# Revit family: 879-103X99-001-DN50-250
name_source: partatom
category: Pipe Accessories
units: mm (PartAtom-declared; Revit-internal decimal feet)

## family parameters
Always vertical = Yes
Cut with Voids When Loaded = No
Part Type = Valve - Breaks Into
Round Connector Dimension = Use Diameter
Shared = No
Work Plane-Based = No

## types (45) — shared parameters
879-0050-10-14400309999 = DN50_PN10/16
879-0050-10-14400319999 = DN50_PN10/16
879-0050-10-144003199A0 = DN50_PN10/16
879-0050-10-14400329999 = DN50_PN10/16
879-0050-10-14400339999 = DN50_PN10/16
879-0065-10-14400309999 = DN65_PN10/16
879-0065-10-14400319999 = DN65_PN10/16
879-0065-10-144003199A0 = DN65_PN10/16
879-0065-10-14400329999 = DN65_PN10/16
879-0065-10-14400339999 = DN65_PN10/16
879-0080-10-14400309999 = DN80_PN10/16
879-0080-10-14400319999 = DN80_PN10/16
879-0080-10-144003199A0 = DN80_PN10/16
879-0080-10-14400329999 = DN80_PN10/16
879-0080-10-14400339999 = DN80_PN10/16
879-0100-10-14400309999 = DN100_PN10/16
879-0100-10-14400319999 = DN100_PN10/16
879-0100-10-144003199A0 = DN100_PN10/16
879-0100-10-14400329999 = DN100_PN10/16
879-0100-10-14400339999 = DN100_PN10/16
879-0150-10-14400309999 = DN150_PN10/16
879-0150-10-14400319999 = DN150_PN10/16
879-0150-10-144003199A0 = DN150_PN10/16
879-0150-10-14400329999 = DN150_PN10/16
879-0150-10-14400339999 = DN150_PN10/16
879-0200-10-04400309999 = DN200_PN10
879-0200-10-04400319999 = DN200_PN10
879-0200-10-044003199A0 = DN200_PN10
879-0200-10-04400329999 = DN200_PN10
879-0200-10-04400339999 = DN200_PN10
879-0200-10-14400309999 = DN200_PN16
879-0200-10-14400319999 = DN200_PN16
879-0200-10-144003199A0 = DN200_PN16
879-0200-10-14400329999 = DN200_PN16
879-0200-10-14400339999 = DN200_PN16
879-0250-10-04400309999 = DN250_PN10
879-0250-10-04400319999 = DN250_PN10
879-0250-10-044003199A0 = DN250_PN10
879-0250-10-04400329999 = DN250_PN10
879-0250-10-04400339999 = DN250_PN10
879-0250-10-14400309999 = DN250_PN16
879-0250-10-14400319999 = DN250_PN16
879-0250-10-144003199A0 = DN250_PN16
879-0250-10-14400329999 = DN250_PN16
879-0250-10-14400339999 = DN250_PN16
Body_wall_thickness = 10 mm  [stored 0.0328084 ft]
Description_ = AVK ONE WAY ALTITUDE LEVEL CONTROL VALVE
Search_Table = 879-103X99-001-DN50-250
URL product pages = https://www.avkvalves.com

## per-type parameters (varying)
- 879-0050-10-14400309999_DN50_PN10/16: Body_Collar_Dia=21 mm  [stored 0.0688976 ft]; Body_Collar_Dia_2=14 mm  [stored 0.0459318 ft]; Body_Flange_Dia=66 mm; Body_Flange_Dia_2=72 mm; Body_Height_1=58 mm; Body_Height_2=29 mm; Body_Height_3=45 mm  [stored 0.147638 ft]; Body_Height_4=44 mm  [stored 0.144357 ft]; Body_Top_Dia=9 mm  [stored 0.0295276 ft]; Body_Top_Dia_2=7 mm  [stored 0.0229659 ft]; Body_With_Dia=29 mm; Body_With_Dia_1=58 mm; Body_With_Dia_2=58 mm; Bolt_support=177 mm; Bolt_support_2=88 mm; Bolt_support_Dia=12 mm  [stored 0.0393701 ft]; Bolt_support_lenght=45 mm  [stored 0.147638 ft]; Bolt_support_lenght_2=55 mm; Bottom_profile=13 mm; D1=50 mm; D3=83 mm; DN=50 mm; Fillet_Length=6 mm  [stored 0.019685 ft]; Fillet_Length_Ref=18 mm  [stored 0.0590551 ft]; Flange_thickness=19 mm  [stored 0.062336 ft]; H=525 mm; H3_Ref=519 mm; ID=25 mm  [stored 0.082021 ft]; L=230 mm; L_Ref=96 mm; NV_Dia=50 mm; PG_Dia=25 mm  [stored 0.082021 ft]; PG_Ref=38 mm; PG_depth=8 mm  [stored 0.0262467 ft]; PG_height=210 mm; PG_height_1=198 mm; PG_ref=35 mm  [stored 0.114829 ft]; PR_1=73 mm; P_lenght=33 mm  [stored 0.108268 ft]; Pilot_Dia_1=15 mm  [stored 0.0492126 ft]; Pilot_Dia_2=30 mm  [stored 0.0984252 ft]; Pilot_Dia_3=10 mm  [stored 0.0328084 ft]; Pilot_Dia_4=5 mm  [stored 0.0164042 ft]; Pilot_Dia_5=3 mm  [stored 0.00984252 ft]; Pilot_top_1=291 mm; Pilot_top_ref=135 mm; Profile1_Height=100 mm; Profile1_Length=22 mm  [stored 0.0721785 ft]; Profile1_Length_2=15 mm  [stored 0.0492126 ft]; Profile_Dia=6 mm  [stored 0.019685 ft]; Profile_Dia_2=6 mm  [stored 0.019685 ft]; Profile_Dia_3=12 mm  [stored 0.0393701 ft]; Profile_Dia_Ref=3 mm  [stored 0.00984252 ft]; Profile_Dia_Ref_2=12 mm  [stored 0.0393701 ft]; Profile_height ref=12 mm  [stored 0.0393701 ft]; T_Height=325 mm; T_Height_2=278 mm; T_Height_Ref_1=46 mm; T_Height_Ref_2=54 mm; T_ref=259 mm; Top_Profile=106 mm; Top_Profile_Ref=111 mm; W=535 mm; W_Ref=527 mm
- 879-0050-10-14400319999_DN50_PN10/16: Body_Collar_Dia=21 mm  [stored 0.0688976 ft]; Body_Collar_Dia_2=14 mm  [stored 0.0459318 ft]; Body_Flange_Dia=66 mm; Body_Flange_Dia_2=72 mm; Body_Height_1=58 mm; Body_Height_2=29 mm; Body_Height_3=50 mm; Body_Height_4=44 mm  [stored 0.144357 ft]; Body_Top_Dia=9 mm  [stored 0.0295276 ft]; Body_Top_Dia_2=7 mm  [stored 0.0229659 ft]; Body_With_Dia=29 mm; Body_With_Dia_1=58 mm; Body_With_Dia_2=58 mm; Bolt_support=177 mm; Bolt_support_2=88 mm; Bolt_support_Dia=12 mm  [stored 0.0393701 ft]; Bolt_support_lenght=45 mm  [stored 0.147638 ft]; Bolt_support_lenght_2=55 mm; Bottom_profile=13 mm; D1=50 mm; D3=83 mm; DN=50 mm; Fillet_Length=6 mm  [stored 0.019685 ft]; Fillet_Length_Ref=18 mm  [stored 0.0590551 ft]; Flange_thickness=19 mm  [stored 0.062336 ft]; H=525 mm; H3_Ref=519 mm; ID=25 mm  [stored 0.082021 ft]; L=230 mm; L_Ref=96 mm; NV_Dia=50 mm; PG_Dia=25 mm  [stored 0.082021 ft]; PG_Ref=38 mm; PG_depth=8 mm  [stored 0.0262467 ft]; PG_height=218 mm; PG_height_1=206 mm; PG_ref=35 mm  [stored 0.114829 ft]; PR_1=71 mm; P_lenght=33 mm  [stored 0.108268 ft]; Pilot_Dia_1=15 mm  [stored 0.0492126 ft]; Pilot_Dia_2=30 mm  [stored 0.0984252 ft]; Pilot_Dia_3=10 mm  [stored 0.0328084 ft]; Pilot_Dia_4=5 mm  [stored 0.0164042 ft]; Pilot_Dia_5=3 mm  [stored 0.00984252 ft]; Pilot_top_1=294 mm; Pilot_top_ref=133 mm; Profile1_Height=110 mm; Profile1_Length=22 mm  [stored 0.0721785 ft]; Profile1_Length_2=15 mm  [stored 0.0492126 ft]; Profile_Dia=6 mm  [stored 0.019685 ft]; Profile_Dia_2=6 mm  [stored 0.019685 ft]; Profile_Dia_3=12 mm  [stored 0.0393701 ft]; Profile_Dia_Ref=3 mm  [stored 0.00984252 ft]; Profile_Dia_Ref_2=12 mm  [stored 0.0393701 ft]; Profile_height ref=12 mm  [stored 0.0393701 ft]; T_Height=315 mm; T_Height_2=270 mm; T_Height_Ref_1=45 mm  [stored 0.147638 ft]; T_Height_Ref_2=52 mm; T_ref=264 mm; Top_Profile=106 mm; Top_Profile_Ref=111 mm; W=535 mm; W_Ref=527 mm
- 879-0050-10-144003199A0_DN50_PN10/16: Body_Collar_Dia=21 mm  [stored 0.0688976 ft]; Body_Collar_Dia_2=14 mm  [stored 0.0459318 ft]; Body_Flange_Dia=66 mm; Body_Flange_Dia_2=72 mm; Body_Height_1=58 mm; Body_Height_2=29 mm; Body_Height_3=45 mm  [stored 0.147638 ft]; Body_Height_4=44 mm  [stored 0.144357 ft]; Body_Top_Dia=9 mm  [stored 0.0295276 ft]; Body_Top_Dia_2=7 mm  [stored 0.0229659 ft]; Body_With_Dia=29 mm; Body_With_Dia_1=58 mm; Body_With_Dia_2=58 mm; Bolt_support=177 mm; Bolt_support_2=88 mm; Bolt_support_Dia=12 mm  [stored 0.0393701 ft]; Bolt_support_lenght=45 mm  [stored 0.147638 ft]; Bolt_support_lenght_2=55 mm; Bottom_profile=13 mm; D1=50 mm; D3=83 mm; DN=50 mm; Fillet_Length=6 mm  [stored 0.019685 ft]; Fillet_Length_Ref=18 mm  [stored 0.0590551 ft]; Flange_thickness=19 mm  [stored 0.062336 ft]; H=525 mm; H3_Ref=519 mm; ID=25 mm  [stored 0.082021 ft]; L=230 mm; L_Ref=96 mm; NV_Dia=50 mm; PG_Dia=25 mm  [stored 0.082021 ft]; PG_Ref=38 mm; PG_depth=8 mm  [stored 0.0262467 ft]; PG_height=210 mm; PG_height_1=198 mm; PG_ref=35 mm  [stored 0.114829 ft]; PR_1=73 mm; P_lenght=33 mm  [stored 0.108268 ft]; Pilot_Dia_1=15 mm  [stored 0.0492126 ft]; Pilot_Dia_2=30 mm  [stored 0.0984252 ft]; Pilot_Dia_3=10 mm  [stored 0.0328084 ft]; Pilot_Dia_4=5 mm  [stored 0.0164042 ft]; Pilot_Dia_5=3 mm  [stored 0.00984252 ft]; Pilot_top_1=291 mm; Pilot_top_ref=135 mm; Profile1_Height=100 mm; Profile1_Length=22 mm  [stored 0.0721785 ft]; Profile1_Length_2=15 mm  [stored 0.0492126 ft]; Profile_Dia=6 mm  [stored 0.019685 ft]; Profile_Dia_2=6 mm  [stored 0.019685 ft]; Profile_Dia_3=12 mm  [stored 0.0393701 ft]; Profile_Dia_Ref=3 mm  [stored 0.00984252 ft]; Profile_Dia_Ref_2=12 mm  [stored 0.0393701 ft]; Profile_height ref=12 mm  [stored 0.0393701 ft]; T_Height=325 mm; T_Height_2=278 mm; T_Height_Ref_1=46 mm; T_Height_Ref_2=54 mm; T_ref=259 mm; Top_Profile=106 mm; Top_Profile_Ref=111 mm; W=535 mm; W_Ref=527 mm
- 879-0050-10-14400329999_DN50_PN10/16: Body_Collar_Dia=21 mm  [stored 0.0688976 ft]; Body_Collar_Dia_2=14 mm  [stored 0.0459318 ft]; Body_Flange_Dia=66 mm; Body_Flange_Dia_2=72 mm; Body_Height_1=58 mm; Body_Height_2=29 mm; Body_Height_3=50 mm; Body_Height_4=44 mm  [stored 0.144357 ft]; Body_Top_Dia=9 mm  [stored 0.0295276 ft]; Body_Top_Dia_2=7 mm  [stored 0.0229659 ft]; Body_With_Dia=29 mm; Body_With_Dia_1=58 mm; Body_With_Dia_2=58 mm; Bolt_support=177 mm; Bolt_support_2=88 mm; Bolt_support_Dia=12 mm  [stored 0.0393701 ft]; Bolt_support_lenght=45 mm  [stored 0.147638 ft]; Bolt_support_lenght_2=55 mm; Bottom_profile=13 mm; D1=50 mm; D3=83 mm; DN=50 mm; Fillet_Length=6 mm  [stored 0.019685 ft]; Fillet_Length_Ref=18 mm  [stored 0.0590551 ft]; Flange_thickness=19 mm  [stored 0.062336 ft]; H=525 mm; H3_Ref=519 mm; ID=25 mm  [stored 0.082021 ft]; L=230 mm; L_Ref=96 mm; NV_Dia=50 mm; PG_Dia=25 mm  [stored 0.082021 ft]; PG_Ref=38 mm; PG_depth=8 mm  [stored 0.0262467 ft]; PG_height=218 mm; PG_height_1=206 mm; PG_ref=35 mm  [stored 0.114829 ft]; PR_1=71 mm; P_lenght=33 mm  [stored 0.108268 ft]; Pilot_Dia_1=15 mm  [stored 0.0492126 ft]; Pilot_Dia_2=30 mm  [stored 0.0984252 ft]; Pilot_Dia_3=10 mm  [stored 0.0328084 ft]; Pilot_Dia_4=5 mm  [stored 0.0164042 ft]; Pilot_Dia_5=3 mm  [stored 0.00984252 ft]; Pilot_top_1=294 mm; Pilot_top_ref=133 mm; Profile1_Height=110 mm; Profile1_Length=22 mm  [stored 0.0721785 ft]; Profile1_Length_2=15 mm  [stored 0.0492126 ft]; Profile_Dia=6 mm  [stored 0.019685 ft]; Profile_Dia_2=6 mm  [stored 0.019685 ft]; Profile_Dia_3=12 mm  [stored 0.0393701 ft]; Profile_Dia_Ref=3 mm  [stored 0.00984252 ft]; Profile_Dia_Ref_2=12 mm  [stored 0.0393701 ft]; Profile_height ref=12 mm  [stored 0.0393701 ft]; T_Height=315 mm; T_Height_2=270 mm; T_Height_Ref_1=45 mm  [stored 0.147638 ft]; T_Height_Ref_2=52 mm; T_ref=264 mm; Top_Profile=106 mm; Top_Profile_Ref=111 mm; W=535 mm; W_Ref=527 mm
- 879-0050-10-14400339999_DN50_PN10/16: Body_Collar_Dia=21 mm  [stored 0.0688976 ft]; Body_Collar_Dia_2=14 mm  [stored 0.0459318 ft]; Body_Flange_Dia=66 mm; Body_Flange_Dia_2=72 mm; Body_Height_1=58 mm; Body_Height_2=29 mm; Body_Height_3=45 mm  [stored 0.147638 ft]; Body_Height_4=44 mm  [stored 0.144357 ft]; Body_Top_Dia=9 mm  [stored 0.0295276 ft]; Body_Top_Dia_2=7 mm  [stored 0.0229659 ft]; Body_With_Dia=29 mm; Body_With_Dia_1=58 mm; Body_With_Dia_2=58 mm; Bolt_support=177 mm; Bolt_support_2=88 mm; Bolt_support_Dia=12 mm  [stored 0.0393701 ft]; Bolt_support_lenght=45 mm  [stored 0.147638 ft]; Bolt_support_lenght_2=55 mm; Bottom_profile=13 mm; D1=50 mm; D3=83 mm; DN=50 mm; Fillet_Length=6 mm  [stored 0.019685 ft]; Fillet_Length_Ref=18 mm  [stored 0.0590551 ft]; Flange_thickness=19 mm  [stored 0.062336 ft]; H=525 mm; H3_Ref=519 mm; ID=25 mm  [stored 0.082021 ft]; L=230 mm; L_Ref=96 mm; NV_Dia=50 mm; PG_Dia=25 mm  [stored 0.082021 ft]; PG_Ref=38 mm; PG_depth=8 mm  [stored 0.0262467 ft]; PG_height=211 mm; PG_height_1=198 mm; PG_ref=35 mm  [stored 0.114829 ft]; PR_1=73 mm; P_lenght=33 mm  [stored 0.108268 ft]; Pilot_Dia_1=15 mm  [stored 0.0492126 ft]; Pilot_Dia_2=30 mm  [stored 0.0984252 ft]; Pilot_Dia_3=10 mm  [stored 0.0328084 ft]; Pilot_Dia_4=5 mm  [stored 0.0164042 ft]; Pilot_Dia_5=3 mm  [stored 0.00984252 ft]; Pilot_top_1=291 mm; Pilot_top_ref=135 mm; Profile1_Height=100 mm; Profile1_Length=22 mm  [stored 0.0721785 ft]; Profile1_Length_2=15 mm  [stored 0.0492126 ft]; Profile_Dia=6 mm  [stored 0.019685 ft]; Profile_Dia_2=6 mm  [stored 0.019685 ft]; Profile_Dia_3=12 mm  [stored 0.0393701 ft]; Profile_Dia_Ref=3 mm  [stored 0.00984252 ft]; Profile_Dia_Ref_2=12 mm  [stored 0.0393701 ft]; Profile_height ref=12 mm  [stored 0.0393701 ft]; T_Height=325 mm; T_Height_2=278 mm; T_Height_Ref_1=46 mm; T_Height_Ref_2=54 mm; T_ref=259 mm; Top_Profile=106 mm; Top_Profile_Ref=111 mm; W=535 mm; W_Ref=527 mm
- 879-0065-10-14400309999_DN65_PN10/16: Body_Collar_Dia=26 mm; Body_Collar_Dia_2=18 mm  [stored 0.0590551 ft]; Body_Flange_Dia=83 mm; Body_Flange_Dia_2=91 mm; Body_Height_1=73 mm; Body_Height_2=36 mm; Body_Height_3=58 mm; Body_Height_4=51 mm; Body_Top_Dia=11 mm; Body_Top_Dia_2=9 mm  [stored 0.0295276 ft]; Body_With_Dia=36 mm; Body_With_Dia_1=73 mm; Body_With_Dia_2=73 mm; Bolt_support=223 mm; Bolt_support_2=112 mm; Bolt_support_Dia=12 mm  [stored 0.0393701 ft]; Bolt_support_lenght=53 mm; Bolt_support_lenght_2=63 mm; Bottom_profile=16 mm  [stored 0.0524934 ft]; D1=59 mm; D3=93 mm; DN=65 mm; Fillet_Length=6 mm  [stored 0.019685 ft]; Fillet_Length_Ref=18 mm  [stored 0.0590551 ft]; Flange_thickness=19 mm  [stored 0.062336 ft]; H=555 mm; H3_Ref=549 mm; ID=33 mm  [stored 0.108268 ft]; L=290 mm; L_Ref=126 mm; NV_Dia=65 mm; PG_Dia=33 mm  [stored 0.108268 ft]; PG_Ref=48 mm; PG_depth=8 mm  [stored 0.0262467 ft]; PG_height=236 mm; PG_height_1=219 mm; PG_ref=43 mm  [stored 0.141076 ft]; PR_1=74 mm; P_lenght=39 mm  [stored 0.127953 ft]; Pilot_Dia_1=18 mm  [stored 0.0590551 ft]; Pilot_Dia_2=35 mm  [stored 0.114829 ft]; Pilot_Dia_3=12 mm  [stored 0.0393701 ft]; Pilot_Dia_4=6 mm  [stored 0.019685 ft]; Pilot_Dia_5=4 mm  [stored 0.0131234 ft]; Pilot_top_1=319 mm; Pilot_top_ref=127 mm; Profile1_Height=117 mm; Profile1_Length=25 mm  [stored 0.082021 ft]; Profile1_Length_2=17 mm; Profile_Dia=6 mm  [stored 0.019685 ft]; Profile_Dia_2=6 mm  [stored 0.019685 ft]; Profile_Dia_3=12 mm  [stored 0.0393701 ft]; Profile_Dia_Ref=3 mm  [stored 0.00984252 ft]; Profile_Dia_Ref_2=12 mm  [stored 0.0393701 ft]; Profile_height ref=12 mm  [stored 0.0393701 ft]; T_Height=328 mm; T_Height_2=281 mm; T_Height_Ref_1=47 mm; T_Height_Ref_2=55 mm; T_ref=277 mm; Top_Profile=134 mm; Top_Profile_Ref=139 mm; W=555 mm; W_Ref=547 mm
- 879-0065-10-14400319999_DN65_PN10/16: Body_Collar_Dia=26 mm; Body_Collar_Dia_2=18 mm  [stored 0.0590551 ft]; Body_Flange_Dia=83 mm; Body_Flange_Dia_2=91 mm; Body_Height_1=73 mm; Body_Height_2=36 mm; Body_Height_3=58 mm; Body_Height_4=51 mm; Body_Top_Dia=11 mm; Body_Top_Dia_2=9 mm  [stored 0.0295276 ft]; Body_With_Dia=36 mm; Body_With_Dia_1=73 mm; Body_With_Dia_2=73 mm; Bolt_support=223 mm; Bolt_support_2=112 mm; Bolt_support_Dia=12 mm  [stored 0.0393701 ft]; Bolt_support_lenght=53 mm; Bolt_support_lenght_2=63 mm; Bottom_profile=16 mm  [stored 0.0524934 ft]; D1=59 mm; D3=93 mm; DN=65 mm; Fillet_Length=6 mm  [stored 0.019685 ft]; Fillet_Length_Ref=18 mm  [stored 0.0590551 ft]; Flange_thickness=19 mm  [stored 0.062336 ft]; H=555 mm; H3_Ref=549 mm; ID=33 mm  [stored 0.108268 ft]; L=290 mm; L_Ref=126 mm; NV_Dia=65 mm; PG_Dia=33 mm  [stored 0.108268 ft]; PG_Ref=48 mm; PG_depth=8 mm  [stored 0.0262467 ft]; PG_height=250 mm; PG_height_1=233 mm; PG_ref=43 mm  [stored 0.141076 ft]; PR_1=70 mm; P_lenght=39 mm  [stored 0.127953 ft]; Pilot_Dia_1=18 mm  [stored 0.0590551 ft]; Pilot_Dia_2=35 mm  [stored 0.114829 ft]; Pilot_Dia_3=12 mm  [stored 0.0393701 ft]; Pilot_Dia_4=6 mm  [stored 0.019685 ft]; Pilot_Dia_5=4 mm  [stored 0.0131234 ft]; Pilot_top_1=319 mm; Pilot_top_ref=127 mm; Profile1_Height=135 mm; Profile1_Length=25 mm  [stored 0.082021 ft]; Profile1_Length_2=17 mm; Profile_Dia=6 mm  [stored 0.019685 ft]; Profile_Dia_2=6 mm  [stored 0.019685 ft]; Profile_Dia_3=12 mm  [stored 0.0393701 ft]; Profile_Dia_Ref=3 mm  [stored 0.00984252 ft]; Profile_Dia_Ref_2=12 mm  [stored 0.0393701 ft]; Profile_height ref=12 mm  [stored 0.0393701 ft]; T_Height=310 mm; T_Height_2=265 mm; T_Height_Ref_1=44 mm  [stored 0.144357 ft]; T_Height_Ref_2=52 mm; T_ref=287 mm; Top_Profile=134 mm; Top_Profile_Ref=139 mm; W=555 mm; W_Ref=547 mm
- 879-0065-10-144003199A0_DN65_PN10/16: Body_Collar_Dia=26 mm; Body_Collar_Dia_2=18 mm  [stored 0.0590551 ft]; Body_Flange_Dia=83 mm; Body_Flange_Dia_2=91 mm; Body_Height_1=73 mm; Body_Height_2=36 mm; Body_Height_3=58 mm; Body_Height_4=51 mm; Body_Top_Dia=11 mm; Body_Top_Dia_2=9 mm  [stored 0.0295276 ft]; Body_With_Dia=36 mm; Body_With_Dia_1=73 mm; Body_With_Dia_2=73 mm; Bolt_support=223 mm; Bolt_support_2=112 mm; Bolt_support_Dia=12 mm  [stored 0.0393701 ft]; Bolt_support_lenght=53 mm; Bolt_support_lenght_2=63 mm; Bottom_profile=16 mm  [stored 0.0524934 ft]; D1=59 mm; D3=93 mm; DN=65 mm; Fillet_Length=6 mm  [stored 0.019685 ft]; Fillet_Length_Ref=18 mm  [stored 0.0590551 ft]; Flange_thickness=19 mm  [stored 0.062336 ft]; H=555 mm; H3_Ref=549 mm; ID=33 mm  [stored 0.108268 ft]; L=290 mm; L_Ref=126 mm; NV_Dia=65 mm; PG_Dia=33 mm  [stored 0.108268 ft]; PG_Ref=48 mm; PG_depth=8 mm  [stored 0.0262467 ft]; PG_height=236 mm; PG_height_1=219 mm; PG_ref=43 mm  [stored 0.141076 ft]; PR_1=74 mm; P_lenght=39 mm  [stored 0.127953 ft]; Pilot_Dia_1=18 mm  [stored 0.0590551 ft]; Pilot_Dia_2=35 mm  [stored 0.114829 ft]; Pilot_Dia_3=12 mm  [stored 0.0393701 ft]; Pilot_Dia_4=6 mm  [stored 0.019685 ft]; Pilot_Dia_5=4 mm  [stored 0.0131234 ft]; Pilot_top_1=319 mm; Pilot_top_ref=127 mm; Profile1_Height=117 mm; Profile1_Length=25 mm  [stored 0.082021 ft]; Profile1_Length_2=17 mm; Profile_Dia=6 mm  [stored 0.019685 ft]; Profile_Dia_2=6 mm  [stored 0.019685 ft]; Profile_Dia_3=12 mm  [stored 0.0393701 ft]; Profile_Dia_Ref=3 mm  [stored 0.00984252 ft]; Profile_Dia_Ref_2=12 mm  [stored 0.0393701 ft]; Profile_height ref=12 mm  [stored 0.0393701 ft]; T_Height=328 mm; T_Height_2=281 mm; T_Height_Ref_1=47 mm; T_Height_Ref_2=55 mm; T_ref=277 mm; Top_Profile=134 mm; Top_Profile_Ref=139 mm; W=555 mm; W_Ref=547 mm
- 879-0065-10-14400329999_DN65_PN10/16: Body_Collar_Dia=26 mm; Body_Collar_Dia_2=18 mm  [stored 0.0590551 ft]; Body_Flange_Dia=83 mm; Body_Flange_Dia_2=91 mm; Body_Height_1=73 mm; Body_Height_2=36 mm; Body_Height_3=73 mm; Body_Height_4=51 mm; Body_Top_Dia=11 mm; Body_Top_Dia_2=9 mm  [stored 0.0295276 ft]; Body_With_Dia=36 mm; Body_With_Dia_1=73 mm; Body_With_Dia_2=73 mm; Bolt_support=223 mm; Bolt_support_2=112 mm; Bolt_support_Dia=12 mm  [stored 0.0393701 ft]; Bolt_support_lenght=53 mm; Bolt_support_lenght_2=63 mm; Bottom_profile=16 mm  [stored 0.0524934 ft]; D1=59 mm; D3=93 mm; DN=65 mm; Fillet_Length=6 mm  [stored 0.019685 ft]; Fillet_Length_Ref=18 mm  [stored 0.0590551 ft]; Flange_thickness=19 mm  [stored 0.062336 ft]; H=555 mm; H3_Ref=549 mm; ID=33 mm  [stored 0.108268 ft]; L=290 mm; L_Ref=126 mm; NV_Dia=65 mm; PG_Dia=33 mm  [stored 0.108268 ft]; PG_Ref=48 mm; PG_depth=8 mm  [stored 0.0262467 ft]; PG_height=250 mm; PG_height_1=233 mm; PG_ref=43 mm  [stored 0.141076 ft]; PR_1=70 mm; P_lenght=39 mm  [stored 0.127953 ft]; Pilot_Dia_1=18 mm  [stored 0.0590551 ft]; Pilot_Dia_2=35 mm  [stored 0.114829 ft]; Pilot_Dia_3=12 mm  [stored 0.0393701 ft]; Pilot_Dia_4=6 mm  [stored 0.019685 ft]; Pilot_Dia_5=4 mm  [stored 0.0131234 ft]; Pilot_top_1=326 mm; Pilot_top_ref=120 mm; Profile1_Height=135 mm; Profile1_Length=25 mm  [stored 0.082021 ft]; Profile1_Length_2=17 mm; Profile_Dia=6 mm  [stored 0.019685 ft]; Profile_Dia_2=6 mm  [stored 0.019685 ft]; Profile_Dia_3=12 mm  [stored 0.0393701 ft]; Profile_Dia_Ref=3 mm  [stored 0.00984252 ft]; Profile_Dia_Ref_2=12 mm  [stored 0.0393701 ft]; Profile_height ref=12 mm  [stored 0.0393701 ft]; T_Height=310 mm; T_Height_2=265 mm; T_Height_Ref_1=44 mm  [stored 0.144357 ft]; T_Height_Ref_2=52 mm; T_ref=287 mm; Top_Profile=134 mm; Top_Profile_Ref=139 mm; W=555 mm; W_Ref=547 mm
- 879-0065-10-14400339999_DN65_PN10/16: Body_Collar_Dia=26 mm; Body_Collar_Dia_2=18 mm  [stored 0.0590551 ft]; Body_Flange_Dia=83 mm; Body_Flange_Dia_2=91 mm; Body_Height_1=73 mm; Body_Height_2=36 mm; Body_Height_3=58 mm; Body_Height_4=51 mm; Body_Top_Dia=11 mm; Body_Top_Dia_2=9 mm  [stored 0.0295276 ft]; Body_With_Dia=36 mm; Body_With_Dia_1=73 mm; Body_With_Dia_2=73 mm; Bolt_support=223 mm; Bolt_support_2=112 mm; Bolt_support_Dia=12 mm  [stored 0.0393701 ft]; Bolt_support_lenght=53 mm; Bolt_support_lenght_2=63 mm; Bottom_profile=16 mm  [stored 0.0524934 ft]; D1=59 mm; D3=93 mm; DN=65 mm; Fillet_Length=6 mm  [stored 0.019685 ft]; Fillet_Length_Ref=18 mm  [stored 0.0590551 ft]; Flange_thickness=19 mm  [stored 0.062336 ft]; H=555 mm; H3_Ref=549 mm; ID=33 mm  [stored 0.108268 ft]; L=290 mm; L_Ref=126 mm; NV_Dia=65 mm; PG_Dia=33 mm  [stored 0.108268 ft]; PG_Ref=48 mm; PG_depth=8 mm  [stored 0.0262467 ft]; PG_height=236 mm; PG_height_1=219 mm; PG_ref=43 mm  [stored 0.141076 ft]; PR_1=74 mm; P_lenght=39 mm  [stored 0.127953 ft]; Pilot_Dia_1=18 mm  [stored 0.0590551 ft]; Pilot_Dia_2=35 mm  [stored 0.114829 ft]; Pilot_Dia_3=12 mm  [stored 0.0393701 ft]; Pilot_Dia_4=6 mm  [stored 0.019685 ft]; Pilot_Dia_5=4 mm  [stored 0.0131234 ft]; Pilot_top_1=319 mm; Pilot_top_ref=127 mm; Profile1_Height=117 mm; Profile1_Length=25 mm  [stored 0.082021 ft]; Profile1_Length_2=17 mm; Profile_Dia=6 mm  [stored 0.019685 ft]; Profile_Dia_2=6 mm  [stored 0.019685 ft]; Profile_Dia_3=12 mm  [stored 0.0393701 ft]; Profile_Dia_Ref=3 mm  [stored 0.00984252 ft]; Profile_Dia_Ref_2=12 mm  [stored 0.0393701 ft]; Profile_height ref=12 mm  [stored 0.0393701 ft]; T_Height=328 mm; T_Height_2=281 mm; T_Height_Ref_1=47 mm; T_Height_Ref_2=55 mm; T_ref=277 mm; Top_Profile=134 mm; Top_Profile_Ref=139 mm; W=555 mm; W_Ref=547 mm
- 879-0080-10-14400309999_DN80_PN10/16: Body_Collar_Dia=28 mm; Body_Collar_Dia_2=19 mm  [stored 0.062336 ft]; Body_Flange_Dia=89 mm; Body_Flange_Dia_2=97 mm; Body_Height_1=78 mm; Body_Height_2=39 mm  [stored 0.127953 ft]; Body_Height_3=62 mm; Body_Height_4=54 mm; Body_Top_Dia=11 mm; Body_Top_Dia_2=10 mm  [stored 0.0328084 ft]; Body_With_Dia=39 mm  [stored 0.127953 ft]; Body_With_Dia_1=78 mm; Body_With_Dia_2=78 mm; Bolt_support=238 mm; Bolt_support_2=119 mm; Bolt_support_Dia=12 mm  [stored 0.0393701 ft]; Bolt_support_lenght=60 mm; Bolt_support_lenght_2=70 mm; Bottom_profile=20 mm  [stored 0.0656168 ft]; D1=66 mm; D3=100 mm; DN=80 mm; Fillet_Length=6 mm  [stored 0.019685 ft]; Fillet_Length_Ref=18 mm  [stored 0.0590551 ft]; Flange_thickness=19 mm  [stored 0.062336 ft]; H=570 mm; H3_Ref=564 mm; ID=40 mm  [stored 0.131234 ft]; L=310 mm; L_Ref=136 mm; NV_Dia=80 mm; PG_Dia=40 mm  [stored 0.131234 ft]; PG_Ref=52 mm; PG_depth=8 mm  [stored 0.0262467 ft]; PG_height=266 mm; PG_height_1=246 mm; PG_ref=50 mm; PR_1=70 mm; P_lenght=43 mm  [stored 0.141076 ft]; Pilot_Dia_1=20 mm  [stored 0.0656168 ft]; Pilot_Dia_2=39 mm  [stored 0.127953 ft]; Pilot_Dia_3=13 mm; Pilot_Dia_4=7 mm  [stored 0.0229659 ft]; Pilot_Dia_5=4 mm  [stored 0.0131234 ft]; Pilot_top_1=329 mm; Pilot_top_ref=125 mm; Profile1_Height=144 mm; Profile1_Length=27 mm; Profile1_Length_2=18 mm  [stored 0.0590551 ft]; Profile_Dia=6 mm  [stored 0.019685 ft]; Profile_Dia_2=6 mm  [stored 0.019685 ft]; Profile_Dia_3=12 mm  [stored 0.0393701 ft]; Profile_Dia_Ref=3 mm  [stored 0.00984252 ft]; Profile_Dia_Ref_2=12 mm  [stored 0.0393701 ft]; Profile_height ref=12 mm  [stored 0.0393701 ft]; T_Height=308 mm; T_Height_2=264 mm; T_Height_Ref_1=44 mm  [stored 0.144357 ft]; T_Height_Ref_2=51 mm; T_ref=295 mm; Top_Profile=143 mm; Top_Profile_Ref=148 mm; W=570 mm; W_Ref=562 mm
- 879-0080-10-14400319999_DN80_PN10/16: Body_Collar_Dia=28 mm; Body_Collar_Dia_2=19 mm  [stored 0.062336 ft]; Body_Flange_Dia=89 mm; Body_Flange_Dia_2=97 mm; Body_Height_1=78 mm; Body_Height_2=39 mm  [stored 0.127953 ft]; Body_Height_3=62 mm; Body_Height_4=54 mm; Body_Top_Dia=11 mm; Body_Top_Dia_2=10 mm  [stored 0.0328084 ft]; Body_With_Dia=39 mm  [stored 0.127953 ft]; Body_With_Dia_1=78 mm; Body_With_Dia_2=78 mm; Bolt_support=238 mm; Bolt_support_2=119 mm; Bolt_support_Dia=12 mm  [stored 0.0393701 ft]; Bolt_support_lenght=60 mm; Bolt_support_lenght_2=70 mm; Bottom_profile=20 mm  [stored 0.0656168 ft]; D1=66 mm; D3=100 mm; DN=80 mm; Fillet_Length=6 mm  [stored 0.019685 ft]; Fillet_Length_Ref=18 mm  [stored 0.0590551 ft]; Flange_thickness=19 mm  [stored 0.062336 ft]; H=570 mm; H3_Ref=564 mm; ID=40 mm  [stored 0.131234 ft]; L=310 mm; L_Ref=136 mm; NV_Dia=80 mm; PG_Dia=40 mm  [stored 0.131234 ft]; PG_Ref=52 mm; PG_depth=8 mm  [stored 0.0262467 ft]; PG_height=257 mm; PG_height_1=237 mm; PG_ref=50 mm; PR_1=72 mm; P_lenght=43 mm  [stored 0.141076 ft]; Pilot_Dia_1=20 mm  [stored 0.0656168 ft]; Pilot_Dia_2=39 mm  [stored 0.127953 ft]; Pilot_Dia_3=13 mm; Pilot_Dia_4=7 mm  [stored 0.0229659 ft]; Pilot_Dia_5=4 mm  [stored 0.0131234 ft]; Pilot_top_1=329 mm; Pilot_top_ref=125 mm; Profile1_Height=133 mm; Profile1_Length=27 mm; Profile1_Length_2=18 mm  [stored 0.0590551 ft]; Profile_Dia=6 mm  [stored 0.019685 ft]; Profile_Dia_2=6 mm  [stored 0.019685 ft]; Profile_Dia_3=12 mm  [stored 0.0393701 ft]; Profile_Dia_Ref=3 mm  [stored 0.00984252 ft]; Profile_Dia_Ref_2=12 mm  [stored 0.0393701 ft]; Profile_height ref=12 mm  [stored 0.0393701 ft]; T_Height=319 mm; T_Height_2=273 mm; T_Height_Ref_1=46 mm; T_Height_Ref_2=53 mm; T_ref=289 mm; Top_Profile=143 mm; Top_Profile_Ref=148 mm; W=570 mm; W_Ref=562 mm
- 879-0080-10-144003199A0_DN80_PN10/16: Body_Collar_Dia=28 mm; Body_Collar_Dia_2=19 mm  [stored 0.062336 ft]; Body_Flange_Dia=89 mm; Body_Flange_Dia_2=97 mm; Body_Height_1=78 mm; Body_Height_2=39 mm  [stored 0.127953 ft]; Body_Height_3=62 mm; Body_Height_4=54 mm; Body_Top_Dia=11 mm; Body_Top_Dia_2=10 mm  [stored 0.0328084 ft]; Body_With_Dia=39 mm  [stored 0.127953 ft]; Body_With_Dia_1=78 mm; Body_With_Dia_2=78 mm; Bolt_support=238 mm; Bolt_support_2=119 mm; Bolt_support_Dia=12 mm  [stored 0.0393701 ft]; Bolt_support_lenght=60 mm; Bolt_support_lenght_2=70 mm; Bottom_profile=20 mm  [stored 0.0656168 ft]; D1=66 mm; D3=100 mm; DN=80 mm; Fillet_Length=6 mm  [stored 0.019685 ft]; Fillet_Length_Ref=18 mm  [stored 0.0590551 ft]; Flange_thickness=19 mm  [stored 0.062336 ft]; H=570 mm; H3_Ref=564 mm; ID=40 mm  [stored 0.131234 ft]; L=310 mm; L_Ref=136 mm; NV_Dia=80 mm; PG_Dia=40 mm  [stored 0.131234 ft]; PG_Ref=52 mm; PG_depth=8 mm  [stored 0.0262467 ft]; PG_height=266 mm; PG_height_1=246 mm; PG_ref=50 mm; PR_1=70 mm; P_lenght=43 mm  [stored 0.141076 ft]; Pilot_Dia_1=20 mm  [stored 0.0656168 ft]; Pilot_Dia_2=39 mm  [stored 0.127953 ft]; Pilot_Dia_3=13 mm; Pilot_Dia_4=7 mm  [stored 0.0229659 ft]; Pilot_Dia_5=4 mm  [stored 0.0131234 ft]; Pilot_top_1=329 mm; Pilot_top_ref=125 mm; Profile1_Height=144 mm; Profile1_Length=27 mm; Profile1_Length_2=18 mm  [stored 0.0590551 ft]; Profile_Dia=6 mm  [stored 0.019685 ft]; Profile_Dia_2=6 mm  [stored 0.019685 ft]; Profile_Dia_3=12 mm  [stored 0.0393701 ft]; Profile_Dia_Ref=3 mm  [stored 0.00984252 ft]; Profile_Dia_Ref_2=12 mm  [stored 0.0393701 ft]; Profile_height ref=12 mm  [stored 0.0393701 ft]; T_Height=308 mm; T_Height_2=264 mm; T_Height_Ref_1=44 mm  [stored 0.144357 ft]; T_Height_Ref_2=51 mm; T_ref=295 mm; Top_Profile=143 mm; Top_Profile_Ref=148 mm; W=570 mm; W_Ref=562 mm
- 879-0080-10-14400329999_DN80_PN10/16: Body_Collar_Dia=28 mm; Body_Collar_Dia_2=19 mm  [stored 0.062336 ft]; Body_Flange_Dia=89 mm; Body_Flange_Dia_2=97 mm; Body_Height_1=78 mm; Body_Height_2=39 mm  [stored 0.127953 ft]; Body_Height_3=78 mm; Body_Height_4=54 mm; Body_Top_Dia=11 mm; Body_Top_Dia_2=10 mm  [stored 0.0328084 ft]; Body_With_Dia=39 mm  [stored 0.127953 ft]; Body_With_Dia_1=78 mm; Body_With_Dia_2=78 mm; Bolt_support=238 mm; Bolt_support_2=119 mm; Bolt_support_Dia=12 mm  [stored 0.0393701 ft]; Bolt_support_lenght=60 mm; Bolt_support_lenght_2=70 mm; Bottom_profile=20 mm  [stored 0.0656168 ft]; D1=66 mm; D3=100 mm; DN=80 mm; Fillet_Length=6 mm  [stored 0.019685 ft]; Fillet_Length_Ref=18 mm  [stored 0.0590551 ft]; Flange_thickness=19 mm  [stored 0.062336 ft]; H=570 mm; H3_Ref=564 mm; ID=40 mm  [stored 0.131234 ft]; L=310 mm; L_Ref=136 mm; NV_Dia=80 mm; PG_Dia=40 mm  [stored 0.131234 ft]; PG_Ref=52 mm; PG_depth=8 mm  [stored 0.0262467 ft]; PG_height=257 mm; PG_height_1=237 mm; PG_ref=50 mm; PR_1=72 mm; P_lenght=43 mm  [stored 0.141076 ft]; Pilot_Dia_1=20 mm  [stored 0.0656168 ft]; Pilot_Dia_2=39 mm  [stored 0.127953 ft]; Pilot_Dia_3=13 mm; Pilot_Dia_4=7 mm  [stored 0.0229659 ft]; Pilot_Dia_5=4 mm  [stored 0.0131234 ft]; Pilot_top_1=336 mm; Pilot_top_ref=118 mm; Profile1_Height=133 mm; Profile1_Length=27 mm; Profile1_Length_2=18 mm  [stored 0.0590551 ft]; Profile_Dia=6 mm  [stored 0.019685 ft]; Profile_Dia_2=6 mm  [stored 0.019685 ft]; Profile_Dia_3=12 mm  [stored 0.0393701 ft]; Profile_Dia_Ref=3 mm  [stored 0.00984252 ft]; Profile_Dia_Ref_2=12 mm  [stored 0.0393701 ft]; Profile_height ref=12 mm  [stored 0.0393701 ft]; T_Height=319 mm; T_Height_2=273 mm; T_Height_Ref_1=46 mm; T_Height_Ref_2=53 mm; T_ref=289 mm; Top_Profile=143 mm; Top_Profile_Ref=148 mm; W=570 mm; W_Ref=562 mm
- 879-0080-10-14400339999_DN80_PN10/16: Body_Collar_Dia=28 mm; Body_Collar_Dia_2=19 mm  [stored 0.062336 ft]; Body_Flange_Dia=89 mm; Body_Flange_Dia_2=97 mm; Body_Height_1=78 mm; Body_Height_2=39 mm  [stored 0.127953 ft]; Body_Height_3=62 mm; Body_Height_4=54 mm; Body_Top_Dia=11 mm; Body_Top_Dia_2=10 mm  [stored 0.0328084 ft]; Body_With_Dia=39 mm  [stored 0.127953 ft]; Body_With_Dia_1=78 mm; Body_With_Dia_2=78 mm; Bolt_support=238 mm; Bolt_support_2=119 mm; Bolt_support_Dia=12 mm  [stored 0.0393701 ft]; Bolt_support_lenght=60 mm; Bolt_support_lenght_2=70 mm; Bottom_profile=20 mm  [stored 0.0656168 ft]; D1=66 mm; D3=100 mm; DN=80 mm; Fillet_Length=6 mm  [stored 0.019685 ft]; Fillet_Length_Ref=18 mm  [stored 0.0590551 ft]; Flange_thickness=19 mm  [stored 0.062336 ft]; H=570 mm; H3_Ref=564 mm; ID=40 mm  [stored 0.131234 ft]; L=310 mm; L_Ref=136 mm; NV_Dia=80 mm; PG_Dia=40 mm  [stored 0.131234 ft]; PG_Ref=52 mm; PG_depth=8 mm  [stored 0.0262467 ft]; PG_height=266 mm; PG_height_1=246 mm; PG_ref=50 mm; PR_1=70 mm; P_lenght=43 mm  [stored 0.141076 ft]; Pilot_Dia_1=20 mm  [stored 0.0656168 ft]; Pilot_Dia_2=39 mm  [stored 0.127953 ft]; Pilot_Dia_3=13 mm; Pilot_Dia_4=7 mm  [stored 0.0229659 ft]; Pilot_Dia_5=4 mm  [stored 0.0131234 ft]; Pilot_top_1=329 mm; Pilot_top_ref=125 mm; Profile1_Height=144 mm; Profile1_Length=27 mm; Profile1_Length_2=18 mm  [stored 0.0590551 ft]; Profile_Dia=6 mm  [stored 0.019685 ft]; Profile_Dia_2=6 mm  [stored 0.019685 ft]; Profile_Dia_3=12 mm  [stored 0.0393701 ft]; Profile_Dia_Ref=3 mm  [stored 0.00984252 ft]; Profile_Dia_Ref_2=12 mm  [stored 0.0393701 ft]; Profile_height ref=12 mm  [stored 0.0393701 ft]; T_Height=308 mm; T_Height_2=264 mm; T_Height_Ref_1=44 mm  [stored 0.144357 ft]; T_Height_Ref_2=51 mm; T_ref=295 mm; Top_Profile=143 mm; Top_Profile_Ref=148 mm; W=570 mm; W_Ref=562 mm
- 879-0100-10-14400309999_DN100_PN10/16: Body_Collar_Dia=32 mm; Body_Collar_Dia_2=22 mm  [stored 0.0721785 ft]; Body_Flange_Dia=100 mm; Body_Flange_Dia_2=109 mm; Body_Height_1=88 mm; Body_Height_2=44 mm  [stored 0.144357 ft]; Body_Height_3=59 mm; Body_Height_4=59 mm; Body_Top_Dia=13 mm; Body_Top_Dia_2=11 mm; Body_With_Dia=44 mm  [stored 0.144357 ft]; Body_With_Dia_1=88 mm; Body_With_Dia_2=88 mm; Bolt_support=269 mm; Bolt_support_2=135 mm; Bolt_support_Dia=12 mm  [stored 0.0393701 ft]; Bolt_support_lenght=70 mm; Bolt_support_lenght_2=80 mm; Bottom_profile=25 mm  [stored 0.082021 ft]; D1=78 mm; D3=110 mm; DN=100 mm; Fillet_Length=6 mm  [stored 0.019685 ft]; Fillet_Length_Ref=18 mm  [stored 0.0590551 ft]; Flange_thickness=19 mm  [stored 0.062336 ft]; H=590 mm; H3_Ref=584 mm; ID=50 mm; L=350 mm; L_Ref=156 mm; NV_Dia=100 mm; PG_Dia=50 mm; PG_Ref=58 mm; PG_depth=8 mm  [stored 0.0262467 ft]; PG_height=283 mm; PG_height_1=258 mm; PG_ref=60 mm; PR_1=71 mm; P_lenght=48 mm; Pilot_Dia_1=22 mm  [stored 0.0721785 ft]; Pilot_Dia_2=44 mm  [stored 0.144357 ft]; Pilot_Dia_3=15 mm  [stored 0.0492126 ft]; Pilot_Dia_4=7 mm  [stored 0.0229659 ft]; Pilot_Dia_5=5 mm  [stored 0.0164042 ft]; Pilot_top_1=339 mm; Pilot_top_ref=125 mm; Profile1_Height=150 mm; Profile1_Length=30 mm  [stored 0.0984252 ft]; Profile1_Length_2=20 mm  [stored 0.0656168 ft]; Profile_Dia=6 mm  [stored 0.019685 ft]; Profile_Dia_2=6 mm  [stored 0.019685 ft]; Profile_Dia_3=12 mm  [stored 0.0393701 ft]; Profile_Dia_Ref=3 mm  [stored 0.00984252 ft]; Profile_Dia_Ref_2=12 mm  [stored 0.0393701 ft]; Profile_height ref=12 mm  [stored 0.0393701 ft]; T_Height=312 mm; T_Height_2=267 mm; T_Height_Ref_1=45 mm  [stored 0.147638 ft]; T_Height_Ref_2=52 mm; T_ref=303 mm; Top_Profile=162 mm; Top_Profile_Ref=167 mm; W=590 mm; W_Ref=582 mm
- 879-0100-10-14400319999_DN100_PN10/16: Body_Collar_Dia=32 mm; Body_Collar_Dia_2=22 mm  [stored 0.0721785 ft]; Body_Flange_Dia=100 mm; Body_Flange_Dia_2=109 mm; Body_Height_1=88 mm; Body_Height_2=44 mm  [stored 0.144357 ft]; Body_Height_3=59 mm; Body_Height_4=59 mm; Body_Top_Dia=13 mm; Body_Top_Dia_2=11 mm; Body_With_Dia=44 mm  [stored 0.144357 ft]; Body_With_Dia_1=88 mm; Body_With_Dia_2=88 mm; Bolt_support=269 mm; Bolt_support_2=135 mm; Bolt_support_Dia=12 mm  [stored 0.0393701 ft]; Bolt_support_lenght=70 mm; Bolt_support_lenght_2=80 mm; Bottom_profile=25 mm  [stored 0.082021 ft]; D1=78 mm; D3=110 mm; DN=100 mm; Fillet_Length=6 mm  [stored 0.019685 ft]; Fillet_Length_Ref=18 mm  [stored 0.0590551 ft]; Flange_thickness=19 mm  [stored 0.062336 ft]; H=590 mm; H3_Ref=584 mm; ID=50 mm; L=350 mm; L_Ref=156 mm; NV_Dia=100 mm; PG_Dia=50 mm; PG_Ref=58 mm; PG_depth=8 mm  [stored 0.0262467 ft]; PG_height=276 mm; PG_height_1=251 mm; PG_ref=60 mm; PR_1=73 mm; P_lenght=48 mm; Pilot_Dia_1=22 mm  [stored 0.0721785 ft]; Pilot_Dia_2=44 mm  [stored 0.144357 ft]; Pilot_Dia_3=15 mm  [stored 0.0492126 ft]; Pilot_Dia_4=7 mm  [stored 0.0229659 ft]; Pilot_Dia_5=5 mm  [stored 0.0164042 ft]; Pilot_top_1=339 mm; Pilot_top_ref=125 mm; Profile1_Height=141 mm; Profile1_Length=30 mm  [stored 0.0984252 ft]; Profile1_Length_2=20 mm  [stored 0.0656168 ft]; Profile_Dia=6 mm  [stored 0.019685 ft]; Profile_Dia_2=6 mm  [stored 0.019685 ft]; Profile_Dia_3=12 mm  [stored 0.0393701 ft]; Profile_Dia_Ref=3 mm  [stored 0.00984252 ft]; Profile_Dia_Ref_2=12 mm  [stored 0.0393701 ft]; Profile_height ref=12 mm  [stored 0.0393701 ft]; T_Height=321 mm; T_Height_2=275 mm; T_Height_Ref_1=46 mm; T_Height_Ref_2=54 mm; T_ref=298 mm; Top_Profile=162 mm; Top_Profile_Ref=167 mm; W=590 mm; W_Ref=582 mm
- 879-0100-10-144003199A0_DN100_PN10/16: Body_Collar_Dia=32 mm; Body_Collar_Dia_2=22 mm  [stored 0.0721785 ft]; Body_Flange_Dia=100 mm; Body_Flange_Dia_2=109 mm; Body_Height_1=88 mm; Body_Height_2=44 mm  [stored 0.144357 ft]; Body_Height_3=59 mm; Body_Height_4=59 mm; Body_Top_Dia=13 mm; Body_Top_Dia_2=11 mm; Body_With_Dia=44 mm  [stored 0.144357 ft]; Body_With_Dia_1=88 mm; Body_With_Dia_2=88 mm; Bolt_support=269 mm; Bolt_support_2=135 mm; Bolt_support_Dia=12 mm  [stored 0.0393701 ft]; Bolt_support_lenght=70 mm; Bolt_support_lenght_2=80 mm; Bottom_profile=25 mm  [stored 0.082021 ft]; D1=78 mm; D3=110 mm; DN=100 mm; Fillet_Length=6 mm  [stored 0.019685 ft]; Fillet_Length_Ref=18 mm  [stored 0.0590551 ft]; Flange_thickness=19 mm  [stored 0.062336 ft]; H=590 mm; H3_Ref=584 mm; ID=50 mm; L=350 mm; L_Ref=156 mm; NV_Dia=100 mm; PG_Dia=50 mm; PG_Ref=58 mm; PG_depth=8 mm  [stored 0.0262467 ft]; PG_height=283 mm; PG_height_1=258 mm; PG_ref=60 mm; PR_1=71 mm; P_lenght=48 mm; Pilot_Dia_1=22 mm  [stored 0.0721785 ft]; Pilot_Dia_2=44 mm  [stored 0.144357 ft]; Pilot_Dia_3=15 mm  [stored 0.0492126 ft]; Pilot_Dia_4=7 mm  [stored 0.0229659 ft]; Pilot_Dia_5=5 mm  [stored 0.0164042 ft]; Pilot_top_1=339 mm; Pilot_top_ref=125 mm; Profile1_Height=150 mm; Profile1_Length=30 mm  [stored 0.0984252 ft]; Profile1_Length_2=20 mm  [stored 0.0656168 ft]; Profile_Dia=6 mm  [stored 0.019685 ft]; Profile_Dia_2=6 mm  [stored 0.019685 ft]; Profile_Dia_3=12 mm  [stored 0.0393701 ft]; Profile_Dia_Ref=3 mm  [stored 0.00984252 ft]; Profile_Dia_Ref_2=12 mm  [stored 0.0393701 ft]; Profile_height ref=12 mm  [stored 0.0393701 ft]; T_Height=312 mm; T_Height_2=267 mm; T_Height_Ref_1=45 mm  [stored 0.147638 ft]; T_Height_Ref_2=52 mm; T_ref=303 mm; Top_Profile=162 mm; Top_Profile_Ref=167 mm; W=590 mm; W_Ref=582 mm
- 879-0100-10-14400329999_DN100_PN10/16: Body_Collar_Dia=32 mm; Body_Collar_Dia_2=22 mm  [stored 0.0721785 ft]; Body_Flange_Dia=100 mm; Body_Flange_Dia_2=109 mm; Body_Height_1=88 mm; Body_Height_2=44 mm  [stored 0.144357 ft]; Body_Height_3=70 mm; Body_Height_4=59 mm; Body_Top_Dia=13 mm; Body_Top_Dia_2=11 mm; Body_With_Dia=44 mm  [stored 0.144357 ft]; Body_With_Dia_1=88 mm; Body_With_Dia_2=88 mm; Bolt_support=269 mm; Bolt_support_2=135 mm; Bolt_support_Dia=12 mm  [stored 0.0393701 ft]; Bolt_support_lenght=70 mm; Bolt_support_lenght_2=80 mm; Bottom_profile=25 mm  [stored 0.082021 ft]; D1=78 mm; D3=110 mm; DN=100 mm; Fillet_Length=6 mm  [stored 0.019685 ft]; Fillet_Length_Ref=18 mm  [stored 0.0590551 ft]; Flange_thickness=19 mm  [stored 0.062336 ft]; H=590 mm; H3_Ref=584 mm; ID=50 mm; L=350 mm; L_Ref=156 mm; NV_Dia=100 mm; PG_Dia=50 mm; PG_Ref=58 mm; PG_depth=8 mm  [stored 0.0262467 ft]; PG_height=276 mm; PG_height_1=251 mm; PG_ref=60 mm; PR_1=73 mm; P_lenght=48 mm; Pilot_Dia_1=22 mm  [stored 0.0721785 ft]; Pilot_Dia_2=44 mm  [stored 0.144357 ft]; Pilot_Dia_3=15 mm  [stored 0.0492126 ft]; Pilot_Dia_4=7 mm  [stored 0.0229659 ft]; Pilot_Dia_5=5 mm  [stored 0.0164042 ft]; Pilot_top_1=345 mm; Pilot_top_ref=119 mm; Profile1_Height=141 mm; Profile1_Length=30 mm  [stored 0.0984252 ft]; Profile1_Length_2=20 mm  [stored 0.0656168 ft]; Profile_Dia=6 mm  [stored 0.019685 ft]; Profile_Dia_2=6 mm  [stored 0.019685 ft]; Profile_Dia_3=12 mm  [stored 0.0393701 ft]; Profile_Dia_Ref=3 mm  [stored 0.00984252 ft]; Profile_Dia_Ref_2=12 mm  [stored 0.0393701 ft]; Profile_height ref=12 mm  [stored 0.0393701 ft]; T_Height=321 mm; T_Height_2=275 mm; T_Height_Ref_1=46 mm; T_Height_Ref_2=54 mm; T_ref=298 mm; Top_Profile=162 mm; Top_Profile_Ref=167 mm; W=590 mm; W_Ref=582 mm
- 879-0100-10-14400339999_DN100_PN10/16: Body_Collar_Dia=32 mm; Body_Collar_Dia_2=22 mm  [stored 0.0721785 ft]; Body_Flange_Dia=100 mm; Body_Flange_Dia_2=109 mm; Body_Height_1=88 mm; Body_Height_2=44 mm  [stored 0.144357 ft]; Body_Height_3=59 mm; Body_Height_4=59 mm; Body_Top_Dia=13 mm; Body_Top_Dia_2=11 mm; Body_With_Dia=44 mm  [stored 0.144357 ft]; Body_With_Dia_1=88 mm; Body_With_Dia_2=88 mm; Bolt_support=269 mm; Bolt_support_2=135 mm; Bolt_support_Dia=12 mm  [stored 0.0393701 ft]; Bolt_support_lenght=70 mm; Bolt_support_lenght_2=80 mm; Bottom_profile=25 mm  [stored 0.082021 ft]; D1=78 mm; D3=110 mm; DN=100 mm; Fillet_Length=6 mm  [stored 0.019685 ft]; Fillet_Length_Ref=18 mm  [stored 0.0590551 ft]; Flange_thickness=19 mm  [stored 0.062336 ft]; H=590 mm; H3_Ref=584 mm; ID=50 mm; L=350 mm; L_Ref=156 mm; NV_Dia=100 mm; PG_Dia=50 mm; PG_Ref=58 mm; PG_depth=8 mm  [stored 0.0262467 ft]; PG_height=283 mm; PG_height_1=258 mm; PG_ref=60 mm; PR_1=71 mm; P_lenght=48 mm; Pilot_Dia_1=22 mm  [stored 0.0721785 ft]; Pilot_Dia_2=44 mm  [stored 0.144357 ft]; Pilot_Dia_3=15 mm  [stored 0.0492126 ft]; Pilot_Dia_4=7 mm  [stored 0.0229659 ft]; Pilot_Dia_5=5 mm  [stored 0.0164042 ft]; Pilot_top_1=339 mm; Pilot_top_ref=125 mm; Profile1_Height=150 mm; Profile1_Length=30 mm  [stored 0.0984252 ft]; Profile1_Length_2=20 mm  [stored 0.0656168 ft]; Profile_Dia=6 mm  [stored 0.019685 ft]; Profile_Dia_2=6 mm  [stored 0.019685 ft]; Profile_Dia_3=12 mm  [stored 0.0393701 ft]; Profile_Dia_Ref=3 mm  [stored 0.00984252 ft]; Profile_Dia_Ref_2=12 mm  [stored 0.0393701 ft]; Profile_height ref=12 mm  [stored 0.0393701 ft]; T_Height=312 mm; T_Height_2=267 mm; T_Height_Ref_1=45 mm  [stored 0.147638 ft]; T_Height_Ref_2=52 mm; T_ref=303 mm; Top_Profile=162 mm; Top_Profile_Ref=167 mm; W=590 mm; W_Ref=582 mm
- 879-0150-10-14400309999_DN150_PN10/16: Body_Collar_Dia=44 mm  [stored 0.144357 ft]; Body_Collar_Dia_2=30 mm  [stored 0.0984252 ft]; Body_Flange_Dia=137 mm; Body_Flange_Dia_2=150 mm; Body_Height_1=120 mm; Body_Height_2=60 mm; Body_Height_3=60 mm; Body_Height_4=75 mm; Body_Top_Dia=18 mm  [stored 0.0590551 ft]; Body_Top_Dia_2=15 mm  [stored 0.0492126 ft]; Body_With_Dia=60 mm; Body_With_Dia_1=120 mm; Body_With_Dia_2=120 mm; Bolt_support=369 mm; Bolt_support_2=185 mm; Bolt_support_Dia=16 mm  [stored 0.0524934 ft]; Bolt_support_lenght=95 mm; Bolt_support_lenght_2=105 mm; Bottom_profile=38 mm; D1=106 mm; D3=143 mm; DN=150 mm; Fillet_Length=8 mm  [stored 0.0262467 ft]; Fillet_Length_Ref=24 mm  [stored 0.0787402 ft]; Flange_thickness=19 mm  [stored 0.062336 ft]; H=725 mm; H3_Ref=717 mm; ID=75 mm; L=480 mm; L_Ref=221 mm; NV_Dia=125 mm; PG_Dia=50 mm; PG_Ref=80 mm; PG_depth=11 mm; PG_height=346 mm; PG_height_1=321 mm; PG_ref=85 mm; PR_1=81 mm; P_lenght=68 mm; Pilot_Dia_1=31 mm  [stored 0.101706 ft]; Pilot_Dia_2=62 mm; Pilot_Dia_3=21 mm  [stored 0.0688976 ft]; Pilot_Dia_4=10 mm  [stored 0.0328084 ft]; Pilot_Dia_5=7 mm  [stored 0.0229659 ft]; Pilot_top_1=415 mm; Pilot_top_ref=150 mm; Profile1_Height=195 mm; Profile1_Length=39 mm  [stored 0.127953 ft]; Profile1_Length_2=26 mm; Profile_Dia=8 mm  [stored 0.0262467 ft]; Profile_Dia_2=8 mm  [stored 0.0262467 ft]; Profile_Dia_3=16 mm  [stored 0.0524934 ft]; Profile_Dia_Ref=4 mm  [stored 0.0131234 ft]; Profile_Dia_Ref_2=16 mm  [stored 0.0524934 ft]; Profile_height ref=20 mm  [stored 0.0656168 ft]; T_Height=360 mm; T_Height_2=308 mm; T_Height_Ref_1=51 mm; T_Height_Ref_2=60 mm; T_ref=378 mm; Top_Profile=222 mm; Top_Profile_Ref=227 mm; W=655 mm; W_Ref=644 mm
- 879-0150-10-14400319999_DN150_PN10/16: Body_Collar_Dia=44 mm  [stored 0.144357 ft]; Body_Collar_Dia_2=30 mm  [stored 0.0984252 ft]; Body_Flange_Dia=137 mm; Body_Flange_Dia_2=150 mm; Body_Height_1=120 mm; Body_Height_2=60 mm; Body_Height_3=68 mm; Body_Height_4=75 mm; Body_Top_Dia=18 mm  [stored 0.0590551 ft]; Body_Top_Dia_2=15 mm  [stored 0.0492126 ft]; Body_With_Dia=60 mm; Body_With_Dia_1=120 mm; Body_With_Dia_2=120 mm; Bolt_support=369 mm; Bolt_support_2=185 mm; Bolt_support_Dia=16 mm  [stored 0.0524934 ft]; Bolt_support_lenght=95 mm; Bolt_support_lenght_2=105 mm; Bottom_profile=38 mm; D1=106 mm; D3=143 mm; DN=150 mm; Fillet_Length=8 mm  [stored 0.0262467 ft]; Fillet_Length_Ref=24 mm  [stored 0.0787402 ft]; Flange_thickness=19 mm  [stored 0.062336 ft]; H=725 mm; H3_Ref=717 mm; ID=75 mm; L=480 mm; L_Ref=221 mm; NV_Dia=125 mm; PG_Dia=50 mm; PG_Ref=80 mm; PG_depth=11 mm; PG_height=346 mm; PG_height_1=321 mm; PG_ref=85 mm; PR_1=81 mm; P_lenght=68 mm; Pilot_Dia_1=31 mm  [stored 0.101706 ft]; Pilot_Dia_2=62 mm; Pilot_Dia_3=21 mm  [stored 0.0688976 ft]; Pilot_Dia_4=10 mm  [stored 0.0328084 ft]; Pilot_Dia_5=7 mm  [stored 0.0229659 ft]; Pilot_top_1=419 mm; Pilot_top_ref=146 mm; Profile1_Height=195 mm; Profile1_Length=39 mm  [stored 0.127953 ft]; Profile1_Length_2=26 mm; Profile_Dia=8 mm  [stored 0.0262467 ft]; Profile_Dia_2=8 mm  [stored 0.0262467 ft]; Profile_Dia_3=16 mm  [stored 0.0524934 ft]; Profile_Dia_Ref=4 mm  [stored 0.0131234 ft]; Profile_Dia_Ref_2=16 mm  [stored 0.0524934 ft]; Profile_height ref=20 mm  [stored 0.0656168 ft]; T_Height=360 mm; T_Height_2=308 mm; T_Height_Ref_1=51 mm; T_Height_Ref_2=60 mm; T_ref=378 mm; Top_Profile=222 mm; Top_Profile_Ref=227 mm; W=655 mm; W_Ref=644 mm
- 879-0150-10-144003199A0_DN150_PN10/16: Body_Collar_Dia=44 mm  [stored 0.144357 ft]; Body_Collar_Dia_2=30 mm  [stored 0.0984252 ft]; Body_Flange_Dia=137 mm; Body_Flange_Dia_2=150 mm; Body_Height_1=120 mm; Body_Height_2=60 mm; Body_Height_3=60 mm; Body_Height_4=75 mm; Body_Top_Dia=18 mm  [stored 0.0590551 ft]; Body_Top_Dia_2=15 mm  [stored 0.0492126 ft]; Body_With_Dia=60 mm; Body_With_Dia_1=120 mm; Body_With_Dia_2=120 mm; Bolt_support=369 mm; Bolt_support_2=185 mm; Bolt_support_Dia=16 mm  [stored 0.0524934 ft]; Bolt_support_lenght=95 mm; Bolt_support_lenght_2=105 mm; Bottom_profile=38 mm; D1=106 mm; D3=143 mm; DN=150 mm; Fillet_Length=8 mm  [stored 0.0262467 ft]; Fillet_Length_Ref=24 mm  [stored 0.0787402 ft]; Flange_thickness=19 mm  [stored 0.062336 ft]; H=725 mm; H3_Ref=717 mm; ID=75 mm; L=480 mm; L_Ref=221 mm; NV_Dia=125 mm; PG_Dia=50 mm; PG_Ref=80 mm; PG_depth=11 mm; PG_height=346 mm; PG_height_1=321 mm; PG_ref=85 mm; PR_1=81 mm; P_lenght=68 mm; Pilot_Dia_1=31 mm  [stored 0.101706 ft]; Pilot_Dia_2=62 mm; Pilot_Dia_3=21 mm  [stored 0.0688976 ft]; Pilot_Dia_4=10 mm  [stored 0.0328084 ft]; Pilot_Dia_5=7 mm  [stored 0.0229659 ft]; Pilot_top_1=415 mm; Pilot_top_ref=150 mm; Profile1_Height=195 mm; Profile1_Length=39 mm  [stored 0.127953 ft]; Profile1_Length_2=26 mm; Profile_Dia=8 mm  [stored 0.0262467 ft]; Profile_Dia_2=8 mm  [stored 0.0262467 ft]; Profile_Dia_3=16 mm  [stored 0.0524934 ft]; Profile_Dia_Ref=4 mm  [stored 0.0131234 ft]; Profile_Dia_Ref_2=16 mm  [stored 0.0524934 ft]; Profile_height ref=20 mm  [stored 0.0656168 ft]; T_Height=360 mm; T_Height_2=308 mm; T_Height_Ref_1=51 mm; T_Height_Ref_2=60 mm; T_ref=378 mm; Top_Profile=222 mm; Top_Profile_Ref=227 mm; W=655 mm; W_Ref=644 mm
- 879-0150-10-14400329999_DN150_PN10/16: Body_Collar_Dia=44 mm  [stored 0.144357 ft]; Body_Collar_Dia_2=30 mm  [stored 0.0984252 ft]; Body_Flange_Dia=137 mm; Body_Flange_Dia_2=150 mm; Body_Height_1=120 mm; Body_Height_2=60 mm; Body_Height_3=68 mm; Body_Height_4=75 mm; Body_Top_Dia=18 mm  [stored 0.0590551 ft]; Body_Top_Dia_2=15 mm  [stored 0.0492126 ft]; Body_With_Dia=60 mm; Body_With_Dia_1=120 mm; Body_With_Dia_2=120 mm; Bolt_support=369 mm; Bolt_support_2=185 mm; Bolt_support_Dia=16 mm  [stored 0.0524934 ft]; Bolt_support_lenght=95 mm; Bolt_support_lenght_2=105 mm; Bottom_profile=38 mm; D1=106 mm; D3=143 mm; DN=150 mm; Fillet_Length=8 mm  [stored 0.0262467 ft]; Fillet_Length_Ref=24 mm  [stored 0.0787402 ft]; Flange_thickness=19 mm  [stored 0.062336 ft]; H=725 mm; H3_Ref=717 mm; ID=75 mm; L=480 mm; L_Ref=221 mm; NV_Dia=125 mm; PG_Dia=50 mm; PG_Ref=80 mm; PG_depth=11 mm; PG_height=346 mm; PG_height_1=321 mm; PG_ref=85 mm; PR_1=81 mm; P_lenght=68 mm; Pilot_Dia_1=31 mm  [stored 0.101706 ft]; Pilot_Dia_2=62 mm; Pilot_Dia_3=21 mm  [stored 0.0688976 ft]; Pilot_Dia_4=10 mm  [stored 0.0328084 ft]; Pilot_Dia_5=7 mm  [stored 0.0229659 ft]; Pilot_top_1=419 mm; Pilot_top_ref=146 mm; Profile1_Height=195 mm; Profile1_Length=39 mm  [stored 0.127953 ft]; Profile1_Length_2=26 mm; Profile_Dia=8 mm  [stored 0.0262467 ft]; Profile_Dia_2=8 mm  [stored 0.0262467 ft]; Profile_Dia_3=16 mm  [stored 0.0524934 ft]; Profile_Dia_Ref=4 mm  [stored 0.0131234 ft]; Profile_Dia_Ref_2=16 mm  [stored 0.0524934 ft]; Profile_height ref=20 mm  [stored 0.0656168 ft]; T_Height=360 mm; T_Height_2=308 mm; T_Height_Ref_1=51 mm; T_Height_Ref_2=60 mm; T_ref=378 mm; Top_Profile=222 mm; Top_Profile_Ref=227 mm; W=655 mm; W_Ref=644 mm
- 879-0150-10-14400339999_DN150_PN10/16: Body_Collar_Dia=44 mm  [stored 0.144357 ft]; Body_Collar_Dia_2=30 mm  [stored 0.0984252 ft]; Body_Flange_Dia=137 mm; Body_Flange_Dia_2=150 mm; Body_Height_1=120 mm; Body_Height_2=60 mm; Body_Height_3=60 mm; Body_Height_4=75 mm; Body_Top_Dia=18 mm  [stored 0.0590551 ft]; Body_Top_Dia_2=15 mm  [stored 0.0492126 ft]; Body_With_Dia=60 mm; Body_With_Dia_1=120 mm; Body_With_Dia_2=120 mm; Bolt_support=369 mm; Bolt_support_2=185 mm; Bolt_support_Dia=16 mm  [stored 0.0524934 ft]; Bolt_support_lenght=95 mm; Bolt_support_lenght_2=105 mm; Bottom_profile=38 mm; D1=106 mm; D3=143 mm; DN=150 mm; Fillet_Length=8 mm  [stored 0.0262467 ft]; Fillet_Length_Ref=24 mm  [stored 0.0787402 ft]; Flange_thickness=19 mm  [stored 0.062336 ft]; H=725 mm; H3_Ref=717 mm; ID=75 mm; L=480 mm; L_Ref=221 mm; NV_Dia=125 mm; PG_Dia=50 mm; PG_Ref=80 mm; PG_depth=11 mm; PG_height=346 mm; PG_height_1=321 mm; PG_ref=85 mm; PR_1=81 mm; P_lenght=68 mm; Pilot_Dia_1=31 mm  [stored 0.101706 ft]; Pilot_Dia_2=62 mm; Pilot_Dia_3=21 mm  [stored 0.0688976 ft]; Pilot_Dia_4=10 mm  [stored 0.0328084 ft]; Pilot_Dia_5=7 mm  [stored 0.0229659 ft]; Pilot_top_1=415 mm; Pilot_top_ref=150 mm; Profile1_Height=195 mm; Profile1_Length=39 mm  [stored 0.127953 ft]; Profile1_Length_2=26 mm; Profile_Dia=8 mm  [stored 0.0262467 ft]; Profile_Dia_2=8 mm  [stored 0.0262467 ft]; Profile_Dia_3=16 mm  [stored 0.0524934 ft]; Profile_Dia_Ref=4 mm  [stored 0.0131234 ft]; Profile_Dia_Ref_2=16 mm  [stored 0.0524934 ft]; Profile_height ref=20 mm  [stored 0.0656168 ft]; T_Height=360 mm; T_Height_2=308 mm; T_Height_Ref_1=51 mm; T_Height_Ref_2=60 mm; T_ref=378 mm; Top_Profile=222 mm; Top_Profile_Ref=227 mm; W=655 mm; W_Ref=644 mm
- 879-0200-10-04400309999_DN200_PN10: Body_Collar_Dia=55 mm; Body_Collar_Dia_2=38 mm; Body_Flange_Dia=171 mm; Body_Flange_Dia_2=188 mm; Body_Height_1=150 mm; Body_Height_2=75 mm; Body_Height_3=75 mm; Body_Height_4=90 mm; Body_Top_Dia=22 mm  [stored 0.0721785 ft]; Body_Top_Dia_2=19 mm  [stored 0.062336 ft]; Body_With_Dia=75 mm; Body_With_Dia_1=150 mm; Body_With_Dia_2=150 mm; Bolt_support=462 mm; Bolt_support_2=231 mm; Bolt_support_Dia=20 mm  [stored 0.0656168 ft]; Bolt_support_lenght=120 mm; Bolt_support_lenght_2=130 mm; Bottom_profile=50 mm; D1=133 mm; D3=170 mm; DN=200 mm; Fillet_Length=10 mm  [stored 0.0328084 ft]; Fillet_Length_Ref=30 mm  [stored 0.0984252 ft]; Flange_thickness=20 mm  [stored 0.0656168 ft]; H=790 mm; H3_Ref=780 mm; ID=100 mm; L=600 mm; L_Ref=280 mm; NV_Dia=125 mm; PG_Dia=67 mm; PG_Ref=100 mm; PG_depth=14 mm  [stored 0.0459318 ft]; PG_height=412 mm; PG_height_1=379 mm; PG_ref=110 mm; PR_1=77 mm; P_lenght=85 mm; Pilot_Dia_1=39 mm  [stored 0.127953 ft]; Pilot_Dia_2=77 mm; Pilot_Dia_3=26 mm; Pilot_Dia_4=13 mm; Pilot_Dia_5=9 mm  [stored 0.0295276 ft]; Pilot_top_1=463 mm; Pilot_top_ref=138 mm; Profile1_Height=238 mm; Profile1_Length=46 mm; Profile1_Length_2=31 mm  [stored 0.101706 ft]; Profile_Dia=10 mm  [stored 0.0328084 ft]; Profile_Dia_2=10 mm  [stored 0.0328084 ft]; Profile_Dia_3=20 mm  [stored 0.0656168 ft]; Profile_Dia_Ref=5 mm  [stored 0.0164042 ft]; Profile_Dia_Ref_2=20 mm  [stored 0.0656168 ft]; Profile_height ref=30 mm  [stored 0.0984252 ft]; T_Height=342 mm; T_Height_2=293 mm; T_Height_Ref_1=49 mm; T_Height_Ref_2=57 mm; T_ref=423 mm; Top_Profile=277 mm; Top_Profile_Ref=282 mm; W=710 mm; W_Ref=696 mm
- 879-0200-10-04400319999_DN200_PN10: Body_Collar_Dia=55 mm; Body_Collar_Dia_2=38 mm; Body_Flange_Dia=171 mm; Body_Flange_Dia_2=188 mm; Body_Height_1=150 mm; Body_Height_2=75 mm; Body_Height_3=100 mm; Body_Height_4=90 mm; Body_Top_Dia=22 mm  [stored 0.0721785 ft]; Body_Top_Dia_2=19 mm  [stored 0.062336 ft]; Body_With_Dia=75 mm; Body_With_Dia_1=150 mm; Body_With_Dia_2=150 mm; Bolt_support=462 mm; Bolt_support_2=231 mm; Bolt_support_Dia=20 mm  [stored 0.0656168 ft]; Bolt_support_lenght=120 mm; Bolt_support_lenght_2=130 mm; Bottom_profile=50 mm; D1=133 mm; D3=170 mm; DN=200 mm; Fillet_Length=10 mm  [stored 0.0328084 ft]; Fillet_Length_Ref=30 mm  [stored 0.0984252 ft]; Flange_thickness=20 mm  [stored 0.0656168 ft]; H=790 mm; H3_Ref=780 mm; ID=100 mm; L=600 mm; L_Ref=280 mm; NV_Dia=125 mm; PG_Dia=67 mm; PG_Ref=100 mm; PG_depth=14 mm  [stored 0.0459318 ft]; PG_height=414 mm; PG_height_1=380 mm; PG_ref=110 mm; PR_1=77 mm; P_lenght=85 mm; Pilot_Dia_1=39 mm  [stored 0.127953 ft]; Pilot_Dia_2=77 mm; Pilot_Dia_3=26 mm; Pilot_Dia_4=13 mm; Pilot_Dia_5=9 mm  [stored 0.0295276 ft]; Pilot_top_1=475 mm; Pilot_top_ref=125 mm; Profile1_Height=240 mm; Profile1_Length=46 mm; Profile1_Length_2=31 mm  [stored 0.101706 ft]; Profile_Dia=10 mm  [stored 0.0328084 ft]; Profile_Dia_2=10 mm  [stored 0.0328084 ft]; Profile_Dia_3=20 mm  [stored 0.0656168 ft]; Profile_Dia_Ref=5 mm  [stored 0.0164042 ft]; Profile_Dia_Ref_2=20 mm  [stored 0.0656168 ft]; Profile_height ref=30 mm  [stored 0.0984252 ft]; T_Height=340 mm; T_Height_2=291 mm; T_Height_Ref_1=49 mm; T_Height_Ref_2=57 mm; T_ref=424 mm; Top_Profile=277 mm; Top_Profile_Ref=282 mm; W=710 mm; W_Ref=696 mm
- 879-0200-10-044003199A0_DN200_PN10: Body_Collar_Dia=55 mm; Body_Collar_Dia_2=38 mm; Body_Flange_Dia=171 mm; Body_Flange_Dia_2=188 mm; Body_Height_1=150 mm; Body_Height_2=75 mm; Body_Height_3=75 mm; Body_Height_4=90 mm; Body_Top_Dia=22 mm  [stored 0.0721785 ft]; Body_Top_Dia_2=19 mm  [stored 0.062336 ft]; Body_With_Dia=75 mm; Body_With_Dia_1=150 mm; Body_With_Dia_2=150 mm; Bolt_support=462 mm; Bolt_support_2=231 mm; Bolt_support_Dia=20 mm  [stored 0.0656168 ft]; Bolt_support_lenght=120 mm; Bolt_support_lenght_2=130 mm; Bottom_profile=50 mm; D1=133 mm; D3=170 mm; DN=200 mm; Fillet_Length=10 mm  [stored 0.0328084 ft]; Fillet_Length_Ref=30 mm  [stored 0.0984252 ft]; Flange_thickness=20 mm  [stored 0.0656168 ft]; H=790 mm; H3_Ref=780 mm; ID=100 mm; L=600 mm; L_Ref=280 mm; NV_Dia=125 mm; PG_Dia=67 mm; PG_Ref=100 mm; PG_depth=14 mm  [stored 0.0459318 ft]; PG_height=412 mm; PG_height_1=379 mm; PG_ref=110 mm; PR_1=77 mm; P_lenght=85 mm; Pilot_Dia_1=39 mm  [stored 0.127953 ft]; Pilot_Dia_2=77 mm; Pilot_Dia_3=26 mm; Pilot_Dia_4=13 mm; Pilot_Dia_5=9 mm  [stored 0.0295276 ft]; Pilot_top_1=463 mm; Pilot_top_ref=138 mm; Profile1_Height=238 mm; Profile1_Length=46 mm; Profile1_Length_2=31 mm  [stored 0.101706 ft]; Profile_Dia=10 mm  [stored 0.0328084 ft]; Profile_Dia_2=10 mm  [stored 0.0328084 ft]; Profile_Dia_3=20 mm  [stored 0.0656168 ft]; Profile_Dia_Ref=5 mm  [stored 0.0164042 ft]; Profile_Dia_Ref_2=20 mm  [stored 0.0656168 ft]; Profile_height ref=30 mm  [stored 0.0984252 ft]; T_Height=342 mm; T_Height_2=293 mm; T_Height_Ref_1=49 mm; T_Height_Ref_2=57 mm; T_ref=423 mm; Top_Profile=277 mm; Top_Profile_Ref=282 mm; W=710 mm; W_Ref=696 mm
- 879-0200-10-04400329999_DN200_PN10: Body_Collar_Dia=55 mm; Body_Collar_Dia_2=38 mm; Body_Flange_Dia=171 mm; Body_Flange_Dia_2=188 mm; Body_Height_1=150 mm; Body_Height_2=75 mm; Body_Height_3=86 mm; Body_Height_4=90 mm; Body_Top_Dia=22 mm  [stored 0.0721785 ft]; Body_Top_Dia_2=19 mm  [stored 0.062336 ft]; Body_With_Dia=75 mm; Body_With_Dia_1=150 mm; Body_With_Dia_2=150 mm; Bolt_support=462 mm; Bolt_support_2=231 mm; Bolt_support_Dia=20 mm  [stored 0.0656168 ft]; Bolt_support_lenght=120 mm; Bolt_support_lenght_2=130 mm; Bottom_profile=50 mm; D1=133 mm; D3=170 mm; DN=200 mm; Fillet_Length=10 mm  [stored 0.0328084 ft]; Fillet_Length_Ref=30 mm  [stored 0.0984252 ft]; Flange_thickness=20 mm  [stored 0.0656168 ft]; H=790 mm; H3_Ref=780 mm; ID=100 mm; L=600 mm; L_Ref=280 mm; NV_Dia=125 mm; PG_Dia=67 mm; PG_Ref=100 mm; PG_depth=14 mm  [stored 0.0459318 ft]; PG_height=414 mm; PG_height_1=380 mm; PG_ref=110 mm; PR_1=77 mm; P_lenght=85 mm; Pilot_Dia_1=39 mm  [stored 0.127953 ft]; Pilot_Dia_2=77 mm; Pilot_Dia_3=26 mm; Pilot_Dia_4=13 mm; Pilot_Dia_5=9 mm  [stored 0.0295276 ft]; Pilot_top_1=468 mm; Pilot_top_ref=132 mm; Profile1_Height=240 mm; Profile1_Length=46 mm; Profile1_Length_2=31 mm  [stored 0.101706 ft]; Profile_Dia=10 mm  [stored 0.0328084 ft]; Profile_Dia_2=10 mm  [stored 0.0328084 ft]; Profile_Dia_3=20 mm  [stored 0.0656168 ft]; Profile_Dia_Ref=5 mm  [stored 0.0164042 ft]; Profile_Dia_Ref_2=20 mm  [stored 0.0656168 ft]; Profile_height ref=30 mm  [stored 0.0984252 ft]; T_Height=340 mm; T_Height_2=291 mm; T_Height_Ref_1=49 mm; T_Height_Ref_2=57 mm; T_ref=424 mm; Top_Profile=277 mm; Top_Profile_Ref=282 mm; W=710 mm; W_Ref=696 mm
- 879-0200-10-04400339999_DN200_PN10: Body_Collar_Dia=55 mm; Body_Collar_Dia_2=38 mm; Body_Flange_Dia=171 mm; Body_Flange_Dia_2=188 mm; Body_Height_1=150 mm; Body_Height_2=75 mm; Body_Height_3=75 mm; Body_Height_4=90 mm; Body_Top_Dia=22 mm  [stored 0.0721785 ft]; Body_Top_Dia_2=19 mm  [stored 0.062336 ft]; Body_With_Dia=75 mm; Body_With_Dia_1=150 mm; Body_With_Dia_2=150 mm; Bolt_support=462 mm; Bolt_support_2=231 mm; Bolt_support_Dia=20 mm  [stored 0.0656168 ft]; Bolt_support_lenght=120 mm; Bolt_support_lenght_2=130 mm; Bottom_profile=50 mm; D1=133 mm; D3=170 mm; DN=200 mm; Fillet_Length=10 mm  [stored 0.0328084 ft]; Fillet_Length_Ref=30 mm  [stored 0.0984252 ft]; Flange_thickness=20 mm  [stored 0.0656168 ft]; H=790 mm; H3_Ref=780 mm; ID=100 mm; L=600 mm; L_Ref=280 mm; NV_Dia=125 mm; PG_Dia=67 mm; PG_Ref=100 mm; PG_depth=14 mm  [stored 0.0459318 ft]; PG_height=412 mm; PG_height_1=379 mm; PG_ref=110 mm; PR_1=77 mm; P_lenght=85 mm; Pilot_Dia_1=39 mm  [stored 0.127953 ft]; Pilot_Dia_2=77 mm; Pilot_Dia_3=26 mm; Pilot_Dia_4=13 mm; Pilot_Dia_5=9 mm  [stored 0.0295276 ft]; Pilot_top_1=463 mm; Pilot_top_ref=138 mm; Profile1_Height=238 mm; Profile1_Length=46 mm; Profile1_Length_2=31 mm  [stored 0.101706 ft]; Profile_Dia=10 mm  [stored 0.0328084 ft]; Profile_Dia_2=10 mm  [stored 0.0328084 ft]; Profile_Dia_3=20 mm  [stored 0.0656168 ft]; Profile_Dia_Ref=5 mm  [stored 0.0164042 ft]; Profile_Dia_Ref_2=20 mm  [stored 0.0656168 ft]; Profile_height ref=30 mm  [stored 0.0984252 ft]; T_Height=342 mm; T_Height_2=293 mm; T_Height_Ref_1=49 mm; T_Height_Ref_2=57 mm; T_ref=423 mm; Top_Profile=277 mm; Top_Profile_Ref=282 mm; W=710 mm; W_Ref=696 mm
- 879-0200-10-14400309999_DN200_PN16: Body_Collar_Dia=55 mm; Body_Collar_Dia_2=38 mm; Body_Flange_Dia=171 mm; Body_Flange_Dia_2=188 mm; Body_Height_1=150 mm; Body_Height_2=75 mm; Body_Height_3=100 mm; Body_Height_4=90 mm; Body_Top_Dia=22 mm  [stored 0.0721785 ft]; Body_Top_Dia_2=19 mm  [stored 0.062336 ft]; Body_With_Dia=75 mm; Body_With_Dia_1=150 mm; Body_With_Dia_2=150 mm; Bolt_support=462 mm; Bolt_support_2=231 mm; Bolt_support_Dia=20 mm  [stored 0.0656168 ft]; Bolt_support_lenght=120 mm; Bolt_support_lenght_2=130 mm; Bottom_profile=50 mm; D1=133 mm; D3=170 mm; DN=201 mm; Fillet_Length=10 mm  [stored 0.0328084 ft]; Fillet_Length_Ref=30 mm  [stored 0.0984252 ft]; Flange_thickness=20 mm  [stored 0.0656168 ft]; H=790 mm; H3_Ref=780 mm; ID=100 mm; L=600 mm; L_Ref=280 mm; NV_Dia=125 mm; PG_Dia=67 mm; PG_Ref=100 mm; PG_depth=14 mm  [stored 0.0459318 ft]; PG_height=414 mm; PG_height_1=380 mm; PG_ref=110 mm; PR_1=77 mm; P_lenght=85 mm; Pilot_Dia_1=39 mm  [stored 0.127953 ft]; Pilot_Dia_2=77 mm; Pilot_Dia_3=26 mm; Pilot_Dia_4=13 mm; Pilot_Dia_5=9 mm  [stored 0.0295276 ft]; Pilot_top_1=475 mm; Pilot_top_ref=125 mm; Profile1_Height=240 mm; Profile1_Length=46 mm; Profile1_Length_2=31 mm  [stored 0.101706 ft]; Profile_Dia=10 mm  [stored 0.0328084 ft]; Profile_Dia_2=10 mm  [stored 0.0328084 ft]; Profile_Dia_3=20 mm  [stored 0.0656168 ft]; Profile_Dia_Ref=5 mm  [stored 0.0164042 ft]; Profile_Dia_Ref_2=20 mm  [stored 0.0656168 ft]; Profile_height ref=30 mm  [stored 0.0984252 ft]; T_Height=340 mm; T_Height_2=291 mm; T_Height_Ref_1=49 mm; T_Height_Ref_2=57 mm; T_ref=424 mm; Top_Profile=277 mm; Top_Profile_Ref=282 mm; W=710 mm; W_Ref=696 mm
- 879-0200-10-14400319999_DN200_PN16: Body_Collar_Dia=55 mm; Body_Collar_Dia_2=38 mm; Body_Flange_Dia=171 mm; Body_Flange_Dia_2=188 mm; Body_Height_1=150 mm; Body_Height_2=75 mm; Body_Height_3=75 mm; Body_Height_4=90 mm; Body_Top_Dia=22 mm  [stored 0.0721785 ft]; Body_Top_Dia_2=19 mm  [stored 0.062336 ft]; Body_With_Dia=75 mm; Body_With_Dia_1=150 mm; Body_With_Dia_2=150 mm; Bolt_support=462 mm; Bolt_support_2=231 mm; Bolt_support_Dia=20 mm  [stored 0.0656168 ft]; Bolt_support_lenght=120 mm; Bolt_support_lenght_2=130 mm; Bottom_profile=50 mm; D1=133 mm; D3=170 mm; DN=201 mm; Fillet_Length=10 mm  [stored 0.0328084 ft]; Fillet_Length_Ref=30 mm  [stored 0.0984252 ft]; Flange_thickness=20 mm  [stored 0.0656168 ft]; H=790 mm; H3_Ref=780 mm; ID=100 mm; L=600 mm; L_Ref=280 mm; NV_Dia=125 mm; PG_Dia=67 mm; PG_Ref=100 mm; PG_depth=14 mm  [stored 0.0459318 ft]; PG_height=412 mm; PG_height_1=379 mm; PG_ref=110 mm; PR_1=77 mm; P_lenght=85 mm; Pilot_Dia_1=39 mm  [stored 0.127953 ft]; Pilot_Dia_2=77 mm; Pilot_Dia_3=26 mm; Pilot_Dia_4=13 mm; Pilot_Dia_5=9 mm  [stored 0.0295276 ft]; Pilot_top_1=463 mm; Pilot_top_ref=138 mm; Profile1_Height=238 mm; Profile1_Length=46 mm; Profile1_Length_2=31 mm  [stored 0.101706 ft]; Profile_Dia=10 mm  [stored 0.0328084 ft]; Profile_Dia_2=10 mm  [stored 0.0328084 ft]; Profile_Dia_3=20 mm  [stored 0.0656168 ft]; Profile_Dia_Ref=5 mm  [stored 0.0164042 ft]; Profile_Dia_Ref_2=20 mm  [stored 0.0656168 ft]; Profile_height ref=30 mm  [stored 0.0984252 ft]; T_Height=342 mm; T_Height_2=293 mm; T_Height_Ref_1=49 mm; T_Height_Ref_2=57 mm; T_ref=423 mm; Top_Profile=277 mm; Top_Profile_Ref=282 mm; W=710 mm; W_Ref=696 mm
- 879-0200-10-144003199A0_DN200_PN16: Body_Collar_Dia=55 mm; Body_Collar_Dia_2=38 mm; Body_Flange_Dia=171 mm; Body_Flange_Dia_2=188 mm; Body_Height_1=150 mm; Body_Height_2=75 mm; Body_Height_3=86 mm; Body_Height_4=90 mm; Body_Top_Dia=22 mm  [stored 0.0721785 ft]; Body_Top_Dia_2=19 mm  [stored 0.062336 ft]; Body_With_Dia=75 mm; Body_With_Dia_1=150 mm; Body_With_Dia_2=150 mm; Bolt_support=462 mm; Bolt_support_2=231 mm; Bolt_support_Dia=20 mm  [stored 0.0656168 ft]; Bolt_support_lenght=120 mm; Bolt_support_lenght_2=130 mm; Bottom_profile=50 mm; D1=133 mm; D3=170 mm; DN=201 mm; Fillet_Length=10 mm  [stored 0.0328084 ft]; Fillet_Length_Ref=30 mm  [stored 0.0984252 ft]; Flange_thickness=20 mm  [stored 0.0656168 ft]; H=790 mm; H3_Ref=780 mm; ID=100 mm; L=600 mm; L_Ref=280 mm; NV_Dia=125 mm; PG_Dia=67 mm; PG_Ref=100 mm; PG_depth=14 mm  [stored 0.0459318 ft]; PG_height=414 mm; PG_height_1=380 mm; PG_ref=110 mm; PR_1=77 mm; P_lenght=85 mm; Pilot_Dia_1=39 mm  [stored 0.127953 ft]; Pilot_Dia_2=77 mm; Pilot_Dia_3=26 mm; Pilot_Dia_4=13 mm; Pilot_Dia_5=9 mm  [stored 0.0295276 ft]; Pilot_top_1=468 mm; Pilot_top_ref=132 mm; Profile1_Height=240 mm; Profile1_Length=46 mm; Profile1_Length_2=31 mm  [stored 0.101706 ft]; Profile_Dia=10 mm  [stored 0.0328084 ft]; Profile_Dia_2=10 mm  [stored 0.0328084 ft]; Profile_Dia_3=20 mm  [stored 0.0656168 ft]; Profile_Dia_Ref=5 mm  [stored 0.0164042 ft]; Profile_Dia_Ref_2=20 mm  [stored 0.0656168 ft]; Profile_height ref=30 mm  [stored 0.0984252 ft]; T_Height=340 mm; T_Height_2=291 mm; T_Height_Ref_1=49 mm; T_Height_Ref_2=57 mm; T_ref=424 mm; Top_Profile=277 mm; Top_Profile_Ref=282 mm; W=710 mm; W_Ref=696 mm
- 879-0200-10-14400329999_DN200_PN16: Body_Collar_Dia=55 mm; Body_Collar_Dia_2=38 mm; Body_Flange_Dia=171 mm; Body_Flange_Dia_2=188 mm; Body_Height_1=150 mm; Body_Height_2=75 mm; Body_Height_3=75 mm; Body_Height_4=90 mm; Body_Top_Dia=22 mm  [stored 0.0721785 ft]; Body_Top_Dia_2=19 mm  [stored 0.062336 ft]; Body_With_Dia=75 mm; Body_With_Dia_1=150 mm; Body_With_Dia_2=150 mm; Bolt_support=462 mm; Bolt_support_2=231 mm; Bolt_support_Dia=20 mm  [stored 0.0656168 ft]; Bolt_support_lenght=120 mm; Bolt_support_lenght_2=130 mm; Bottom_profile=50 mm; D1=133 mm; D3=170 mm; DN=201 mm; Fillet_Length=10 mm  [stored 0.0328084 ft]; Fillet_Length_Ref=30 mm  [stored 0.0984252 ft]; Flange_thickness=20 mm  [stored 0.0656168 ft]; H=790 mm; H3_Ref=780 mm; ID=100 mm; L=600 mm; L_Ref=280 mm; NV_Dia=125 mm; PG_Dia=67 mm; PG_Ref=100 mm; PG_depth=14 mm  [stored 0.0459318 ft]; PG_height=412 mm; PG_height_1=379 mm; PG_ref=110 mm; PR_1=77 mm; P_lenght=85 mm; Pilot_Dia_1=39 mm  [stored 0.127953 ft]; Pilot_Dia_2=77 mm; Pilot_Dia_3=26 mm; Pilot_Dia_4=13 mm; Pilot_Dia_5=9 mm  [stored 0.0295276 ft]; Pilot_top_1=463 mm; Pilot_top_ref=138 mm; Profile1_Height=238 mm; Profile1_Length=46 mm; Profile1_Length_2=31 mm  [stored 0.101706 ft]; Profile_Dia=10 mm  [stored 0.0328084 ft]; Profile_Dia_2=10 mm  [stored 0.0328084 ft]; Profile_Dia_3=20 mm  [stored 0.0656168 ft]; Profile_Dia_Ref=5 mm  [stored 0.0164042 ft]; Profile_Dia_Ref_2=20 mm  [stored 0.0656168 ft]; Profile_height ref=30 mm  [stored 0.0984252 ft]; T_Height=342 mm; T_Height_2=293 mm; T_Height_Ref_1=49 mm; T_Height_Ref_2=57 mm; T_ref=423 mm; Top_Profile=277 mm; Top_Profile_Ref=282 mm; W=710 mm; W_Ref=696 mm
- 879-0200-10-14400339999_DN200_PN16: Body_Collar_Dia=55 mm; Body_Collar_Dia_2=38 mm; Body_Flange_Dia=171 mm; Body_Flange_Dia_2=188 mm; Body_Height_1=150 mm; Body_Height_2=75 mm; Body_Height_3=100 mm; Body_Height_4=90 mm; Body_Top_Dia=22 mm  [stored 0.0721785 ft]; Body_Top_Dia_2=19 mm  [stored 0.062336 ft]; Body_With_Dia=75 mm; Body_With_Dia_1=150 mm; Body_With_Dia_2=150 mm; Bolt_support=462 mm; Bolt_support_2=231 mm; Bolt_support_Dia=20 mm  [stored 0.0656168 ft]; Bolt_support_lenght=120 mm; Bolt_support_lenght_2=130 mm; Bottom_profile=50 mm; D1=133 mm; D3=170 mm; DN=201 mm; Fillet_Length=10 mm  [stored 0.0328084 ft]; Fillet_Length_Ref=30 mm  [stored 0.0984252 ft]; Flange_thickness=20 mm  [stored 0.0656168 ft]; H=790 mm; H3_Ref=780 mm; ID=100 mm; L=600 mm; L_Ref=280 mm; NV_Dia=125 mm; PG_Dia=67 mm; PG_Ref=100 mm; PG_depth=14 mm  [stored 0.0459318 ft]; PG_height=414 mm; PG_height_1=380 mm; PG_ref=110 mm; PR_1=77 mm; P_lenght=85 mm; Pilot_Dia_1=39 mm  [stored 0.127953 ft]; Pilot_Dia_2=77 mm; Pilot_Dia_3=26 mm; Pilot_Dia_4=13 mm; Pilot_Dia_5=9 mm  [stored 0.0295276 ft]; Pilot_top_1=475 mm; Pilot_top_ref=125 mm; Profile1_Height=240 mm; Profile1_Length=46 mm; Profile1_Length_2=31 mm  [stored 0.101706 ft]; Profile_Dia=10 mm  [stored 0.0328084 ft]; Profile_Dia_2=10 mm  [stored 0.0328084 ft]; Profile_Dia_3=20 mm  [stored 0.0656168 ft]; Profile_Dia_Ref=5 mm  [stored 0.0164042 ft]; Profile_Dia_Ref_2=20 mm  [stored 0.0656168 ft]; Profile_height ref=30 mm  [stored 0.0984252 ft]; T_Height=340 mm; T_Height_2=291 mm; T_Height_Ref_1=49 mm; T_Height_Ref_2=57 mm; T_ref=424 mm; Top_Profile=277 mm; Top_Profile_Ref=282 mm; W=710 mm; W_Ref=696 mm
- 879-0250-10-04400309999_DN250_PN10: Body_Collar_Dia=66 mm; Body_Collar_Dia_2=46 mm; Body_Flange_Dia=209 mm; Body_Flange_Dia_2=228 mm; Body_Height_1=183 mm; Body_Height_2=91 mm; Body_Height_3=81 mm; Body_Height_4=106 mm; Body_Top_Dia=27 mm; Body_Top_Dia_2=23 mm  [stored 0.0754593 ft]; Body_With_Dia=91 mm; Body_With_Dia_1=183 mm; Body_With_Dia_2=183 mm; Bolt_support=562 mm; Bolt_support_2=281 mm; Bolt_support_Dia=20 mm  [stored 0.0656168 ft]; Bolt_support_lenght=145 mm; Bolt_support_lenght_2=155 mm; Bottom_profile=63 mm; D1=160 mm; D3=198 mm; DN=250 mm; Fillet_Length=10 mm  [stored 0.0328084 ft]; Fillet_Length_Ref=30 mm  [stored 0.0984252 ft]; Flange_thickness=22 mm  [stored 0.0721785 ft]; H=850 mm; H3_Ref=840 mm; ID=125 mm; L=730 mm; L_Ref=343 mm; NV_Dia=170 mm; PG_Dia=83 mm; PG_Ref=122 mm; PG_depth=14 mm  [stored 0.0459318 ft]; PG_height=478 mm; PG_height_1=436 mm; PG_ref=135 mm; PR_1=72 mm; P_lenght=101 mm; Pilot_Dia_1=46 mm; Pilot_Dia_2=92 mm; Pilot_Dia_3=31 mm  [stored 0.101706 ft]; Pilot_Dia_4=15 mm  [stored 0.0492126 ft]; Pilot_Dia_5=10 mm  [stored 0.0328084 ft]; Pilot_top_1=506 mm; Pilot_top_ref=126 mm; Profile1_Height=292 mm; Profile1_Length=53 mm; Profile1_Length_2=36 mm; Profile_Dia=10 mm  [stored 0.0328084 ft]; Profile_Dia_2=10 mm  [stored 0.0328084 ft]; Profile_Dia_3=20 mm  [stored 0.0656168 ft]; Profile_Dia_Ref=5 mm  [stored 0.0164042 ft]; Profile_Dia_Ref_2=20 mm  [stored 0.0656168 ft]; Profile_height ref=30 mm  [stored 0.0984252 ft]; T_Height=321 mm; T_Height_2=275 mm; T_Height_Ref_1=46 mm; T_Height_Ref_2=53 mm; T_ref=467 mm; Top_Profile=337 mm; Top_Profile_Ref=342 mm; W=775 mm; W_Ref=761 mm
- 879-0250-10-04400319999_DN250_PN10: Body_Collar_Dia=66 mm; Body_Collar_Dia_2=46 mm; Body_Flange_Dia=209 mm; Body_Flange_Dia_2=228 mm; Body_Height_1=183 mm; Body_Height_2=91 mm; Body_Height_3=105 mm; Body_Height_4=106 mm; Body_Top_Dia=27 mm; Body_Top_Dia_2=23 mm  [stored 0.0754593 ft]; Body_With_Dia=91 mm; Body_With_Dia_1=183 mm; Body_With_Dia_2=183 mm; Bolt_support=562 mm; Bolt_support_2=281 mm; Bolt_support_Dia=20 mm  [stored 0.0656168 ft]; Bolt_support_lenght=145 mm; Bolt_support_lenght_2=155 mm; Bottom_profile=63 mm; D1=160 mm; D3=198 mm; DN=250 mm; Fillet_Length=10 mm  [stored 0.0328084 ft]; Fillet_Length_Ref=30 mm  [stored 0.0984252 ft]; Flange_thickness=22 mm  [stored 0.0721785 ft]; H=850 mm; H3_Ref=840 mm; ID=125 mm; L=730 mm; L_Ref=343 mm; NV_Dia=170 mm; PG_Dia=83 mm; PG_Ref=122 mm; PG_depth=14 mm  [stored 0.0459318 ft]; PG_height=480 mm; PG_height_1=438 mm; PG_ref=135 mm; PR_1=72 mm; P_lenght=101 mm; Pilot_Dia_1=46 mm; Pilot_Dia_2=92 mm; Pilot_Dia_3=31 mm  [stored 0.101706 ft]; Pilot_Dia_4=15 mm  [stored 0.0492126 ft]; Pilot_Dia_5=10 mm  [stored 0.0328084 ft]; Pilot_top_1=518 mm; Pilot_top_ref=115 mm; Profile1_Height=295 mm; Profile1_Length=53 mm; Profile1_Length_2=36 mm; Profile_Dia=10 mm  [stored 0.0328084 ft]; Profile_Dia_2=10 mm  [stored 0.0328084 ft]; Profile_Dia_3=20 mm  [stored 0.0656168 ft]; Profile_Dia_Ref=5 mm  [stored 0.0164042 ft]; Profile_Dia_Ref_2=20 mm  [stored 0.0656168 ft]; Profile_height ref=30 mm  [stored 0.0984252 ft]; T_Height=318 mm; T_Height_2=272 mm; T_Height_Ref_1=45 mm  [stored 0.147638 ft]; T_Height_Ref_2=53 mm; T_ref=469 mm; Top_Profile=337 mm; Top_Profile_Ref=342 mm; W=775 mm; W_Ref=761 mm
- 879-0250-10-044003199A0_DN250_PN10: Body_Collar_Dia=66 mm; Body_Collar_Dia_2=46 mm; Body_Flange_Dia=209 mm; Body_Flange_Dia_2=228 mm; Body_Height_1=183 mm; Body_Height_2=91 mm; Body_Height_3=81 mm; Body_Height_4=106 mm; Body_Top_Dia=27 mm; Body_Top_Dia_2=23 mm  [stored 0.0754593 ft]; Body_With_Dia=91 mm; Body_With_Dia_1=183 mm; Body_With_Dia_2=183 mm; Bolt_support=562 mm; Bolt_support_2=281 mm; Bolt_support_Dia=20 mm  [stored 0.0656168 ft]; Bolt_support_lenght=145 mm; Bolt_support_lenght_2=155 mm; Bottom_profile=63 mm; D1=160 mm; D3=198 mm; DN=250 mm; Fillet_Length=10 mm  [stored 0.0328084 ft]; Fillet_Length_Ref=30 mm  [stored 0.0984252 ft]; Flange_thickness=22 mm  [stored 0.0721785 ft]; H=854 mm; H3_Ref=844 mm; ID=125 mm; L=730 mm; L_Ref=343 mm; NV_Dia=170 mm; PG_Dia=83 mm; PG_Ref=122 mm; PG_depth=14 mm  [stored 0.0459318 ft]; PG_height=485 mm; PG_height_1=443 mm; PG_ref=135 mm; PR_1=72 mm; P_lenght=103 mm; Pilot_Dia_1=47 mm; Pilot_Dia_2=94 mm; Pilot_Dia_3=31 mm  [stored 0.101706 ft]; Pilot_Dia_4=16 mm  [stored 0.0524934 ft]; Pilot_Dia_5=10 mm  [stored 0.0328084 ft]; Pilot_top_1=508 mm; Pilot_top_ref=128 mm; Profile1_Height=300 mm; Profile1_Length=53 mm; Profile1_Length_2=36 mm; Profile_Dia=10 mm  [stored 0.0328084 ft]; Profile_Dia_2=10 mm  [stored 0.0328084 ft]; Profile_Dia_3=20 mm  [stored 0.0656168 ft]; Profile_Dia_Ref=5 mm  [stored 0.0164042 ft]; Profile_Dia_Ref_2=20 mm  [stored 0.0656168 ft]; Profile_height ref=30 mm  [stored 0.0984252 ft]; T_Height=317 mm; T_Height_2=271 mm; T_Height_Ref_1=45 mm  [stored 0.147638 ft]; T_Height_Ref_2=53 mm; T_ref=473 mm; Top_Profile=337 mm; Top_Profile_Ref=342 mm; W=775 mm; W_Ref=761 mm
- 879-0250-10-04400329999_DN250_PN10: Body_Collar_Dia=66 mm; Body_Collar_Dia_2=46 mm; Body_Flange_Dia=209 mm; Body_Flange_Dia_2=228 mm; Body_Height_1=183 mm; Body_Height_2=91 mm; Body_Height_3=81 mm; Body_Height_4=106 mm; Body_Top_Dia=27 mm; Body_Top_Dia_2=23 mm  [stored 0.0754593 ft]; Body_With_Dia=91 mm; Body_With_Dia_1=183 mm; Body_With_Dia_2=183 mm; Bolt_support=562 mm; Bolt_support_2=281 mm; Bolt_support_Dia=20 mm  [stored 0.0656168 ft]; Bolt_support_lenght=145 mm; Bolt_support_lenght_2=155 mm; Bottom_profile=63 mm; D1=160 mm; D3=198 mm; DN=250 mm; Fillet_Length=10 mm  [stored 0.0328084 ft]; Fillet_Length_Ref=30 mm  [stored 0.0984252 ft]; Flange_thickness=22 mm  [stored 0.0721785 ft]; H=850 mm; H3_Ref=840 mm; ID=125 mm; L=730 mm; L_Ref=343 mm; NV_Dia=170 mm; PG_Dia=83 mm; PG_Ref=122 mm; PG_depth=14 mm  [stored 0.0459318 ft]; PG_height=496 mm; PG_height_1=454 mm; PG_ref=135 mm; PR_1=67 mm; P_lenght=103 mm; Pilot_Dia_1=47 mm; Pilot_Dia_2=94 mm; Pilot_Dia_3=31 mm  [stored 0.101706 ft]; Pilot_Dia_4=16 mm  [stored 0.0524934 ft]; Pilot_Dia_5=10 mm  [stored 0.0328084 ft]; Pilot_top_1=506 mm; Pilot_top_ref=126 mm; Profile1_Height=315 mm; Profile1_Length=53 mm; Profile1_Length_2=36 mm; Profile_Dia=10 mm  [stored 0.0328084 ft]; Profile_Dia_2=10 mm  [stored 0.0328084 ft]; Profile_Dia_3=20 mm  [stored 0.0656168 ft]; Profile_Dia_Ref=5 mm  [stored 0.0164042 ft]; Profile_Dia_Ref_2=20 mm  [stored 0.0656168 ft]; Profile_height ref=30 mm  [stored 0.0984252 ft]; T_Height=298 mm; T_Height_2=255 mm; T_Height_Ref_1=43 mm  [stored 0.141076 ft]; T_Height_Ref_2=50 mm; T_ref=480 mm; Top_Profile=337 mm; Top_Profile_Ref=342 mm; W=775 mm; W_Ref=761 mm
- 879-0250-10-04400339999_DN250_PN10: Body_Collar_Dia=66 mm; Body_Collar_Dia_2=46 mm; Body_Flange_Dia=209 mm; Body_Flange_Dia_2=228 mm; Body_Height_1=183 mm; Body_Height_2=91 mm; Body_Height_3=81 mm; Body_Height_4=106 mm; Body_Top_Dia=27 mm; Body_Top_Dia_2=23 mm  [stored 0.0754593 ft]; Body_With_Dia=91 mm; Body_With_Dia_1=183 mm; Body_With_Dia_2=183 mm; Bolt_support=562 mm; Bolt_support_2=281 mm; Bolt_support_Dia=20 mm  [stored 0.0656168 ft]; Bolt_support_lenght=145 mm; Bolt_support_lenght_2=155 mm; Bottom_profile=63 mm; D1=160 mm; D3=198 mm; DN=250 mm; Fillet_Length=10 mm  [stored 0.0328084 ft]; Fillet_Length_Ref=30 mm  [stored 0.0984252 ft]; Flange_thickness=22 mm  [stored 0.0721785 ft]; H=850 mm; H3_Ref=840 mm; ID=125 mm; L=730 mm; L_Ref=343 mm; NV_Dia=170 mm; PG_Dia=83 mm; PG_Ref=122 mm; PG_depth=14 mm  [stored 0.0459318 ft]; PG_height=478 mm; PG_height_1=436 mm; PG_ref=135 mm; PR_1=72 mm; P_lenght=101 mm; Pilot_Dia_1=46 mm; Pilot_Dia_2=92 mm; Pilot_Dia_3=31 mm  [stored 0.101706 ft]; Pilot_Dia_4=15 mm  [stored 0.0492126 ft]; Pilot_Dia_5=10 mm  [stored 0.0328084 ft]; Pilot_top_1=506 mm; Pilot_top_ref=126 mm; Profile1_Height=292 mm; Profile1_Length=53 mm; Profile1_Length_2=36 mm; Profile_Dia=10 mm  [stored 0.0328084 ft]; Profile_Dia_2=10 mm  [stored 0.0328084 ft]; Profile_Dia_3=20 mm  [stored 0.0656168 ft]; Profile_Dia_Ref=5 mm  [stored 0.0164042 ft]; Profile_Dia_Ref_2=20 mm  [stored 0.0656168 ft]; Profile_height ref=30 mm  [stored 0.0984252 ft]; T_Height=321 mm; T_Height_2=275 mm; T_Height_Ref_1=46 mm; T_Height_Ref_2=53 mm; T_ref=467 mm; Top_Profile=337 mm; Top_Profile_Ref=342 mm; W=775 mm; W_Ref=761 mm
- 879-0250-10-14400309999_DN250_PN16: Body_Collar_Dia=66 mm; Body_Collar_Dia_2=46 mm; Body_Flange_Dia=209 mm; Body_Flange_Dia_2=228 mm; Body_Height_1=183 mm; Body_Height_2=91 mm; Body_Height_3=105 mm; Body_Height_4=106 mm; Body_Top_Dia=27 mm; Body_Top_Dia_2=23 mm  [stored 0.0754593 ft]; Body_With_Dia=91 mm; Body_With_Dia_1=183 mm; Body_With_Dia_2=183 mm; Bolt_support=562 mm; Bolt_support_2=281 mm; Bolt_support_Dia=20 mm  [stored 0.0656168 ft]; Bolt_support_lenght=145 mm; Bolt_support_lenght_2=155 mm; Bottom_profile=63 mm; D1=160 mm; D3=203 mm; DN=251 mm; Fillet_Length=10 mm  [stored 0.0328084 ft]; Fillet_Length_Ref=30 mm  [stored 0.0984252 ft]; Flange_thickness=22 mm  [stored 0.0721785 ft]; H=850 mm; H3_Ref=840 mm; ID=125 mm; L=730 mm; L_Ref=343 mm; NV_Dia=170 mm; PG_Dia=84 mm; PG_Ref=122 mm; PG_depth=14 mm  [stored 0.0459318 ft]; PG_height=479 mm; PG_height_1=437 mm; PG_ref=135 mm; PR_1=71 mm; P_lenght=101 mm; Pilot_Dia_1=46 mm; Pilot_Dia_2=92 mm; Pilot_Dia_3=31 mm  [stored 0.101706 ft]; Pilot_Dia_4=15 mm  [stored 0.0492126 ft]; Pilot_Dia_5=10 mm  [stored 0.0328084 ft]; Pilot_top_1=515 mm; Pilot_top_ref=112 mm; Profile1_Height=295 mm; Profile1_Length=55 mm; Profile1_Length_2=36 mm; Profile_Dia=10 mm  [stored 0.0328084 ft]; Profile_Dia_2=10 mm  [stored 0.0328084 ft]; Profile_Dia_3=20 mm  [stored 0.0656168 ft]; Profile_Dia_Ref=5 mm  [stored 0.0164042 ft]; Profile_Dia_Ref_2=20 mm  [stored 0.0656168 ft]; Profile_height ref=30 mm  [stored 0.0984252 ft]; T_Height=313 mm; T_Height_2=268 mm; T_Height_Ref_1=45 mm  [stored 0.147638 ft]; T_Height_Ref_2=52 mm; T_ref=466 mm; Top_Profile=337 mm; Top_Profile_Ref=342 mm; W=775 mm; W_Ref=761 mm
- 879-0250-10-14400319999_DN250_PN16: Body_Collar_Dia=66 mm; Body_Collar_Dia_2=46 mm; Body_Flange_Dia=209 mm; Body_Flange_Dia_2=228 mm; Body_Height_1=183 mm; Body_Height_2=91 mm; Body_Height_3=81 mm; Body_Height_4=106 mm; Body_Top_Dia=27 mm; Body_Top_Dia_2=23 mm  [stored 0.0754593 ft]; Body_With_Dia=91 mm; Body_With_Dia_1=183 mm; Body_With_Dia_2=183 mm; Bolt_support=562 mm; Bolt_support_2=281 mm; Bolt_support_Dia=20 mm  [stored 0.0656168 ft]; Bolt_support_lenght=145 mm; Bolt_support_lenght_2=155 mm; Bottom_profile=63 mm; D1=160 mm; D3=203 mm; DN=251 mm; Fillet_Length=10 mm  [stored 0.0328084 ft]; Fillet_Length_Ref=30 mm  [stored 0.0984252 ft]; Flange_thickness=22 mm  [stored 0.0721785 ft]; H=850 mm; H3_Ref=840 mm; ID=125 mm; L=730 mm; L_Ref=343 mm; NV_Dia=170 mm; PG_Dia=84 mm; PG_Ref=122 mm; PG_depth=14 mm  [stored 0.0459318 ft]; PG_height=483 mm; PG_height_1=441 mm; PG_ref=135 mm; PR_1=70 mm; P_lenght=103 mm; Pilot_Dia_1=47 mm; Pilot_Dia_2=94 mm; Pilot_Dia_3=31 mm  [stored 0.101706 ft]; Pilot_Dia_4=16 mm  [stored 0.0524934 ft]; Pilot_Dia_5=10 mm  [stored 0.0328084 ft]; Pilot_top_1=504 mm; Pilot_top_ref=124 mm; Profile1_Height=300 mm; Profile1_Length=55 mm; Profile1_Length_2=36 mm; Profile_Dia=10 mm  [stored 0.0328084 ft]; Profile_Dia_2=10 mm  [stored 0.0328084 ft]; Profile_Dia_3=20 mm  [stored 0.0656168 ft]; Profile_Dia_Ref=5 mm  [stored 0.0164042 ft]; Profile_Dia_Ref_2=20 mm  [stored 0.0656168 ft]; Profile_height ref=30 mm  [stored 0.0984252 ft]; T_Height=308 mm; T_Height_2=264 mm; T_Height_Ref_1=44 mm  [stored 0.144357 ft]; T_Height_Ref_2=51 mm; T_ref=469 mm; Top_Profile=337 mm; Top_Profile_Ref=342 mm; W=775 mm; W_Ref=761 mm
- 879-0250-10-144003199A0_DN250_PN16: Body_Collar_Dia=66 mm; Body_Collar_Dia_2=46 mm; Body_Flange_Dia=209 mm; Body_Flange_Dia_2=228 mm; Body_Height_1=183 mm; Body_Height_2=91 mm; Body_Height_3=81 mm; Body_Height_4=106 mm; Body_Top_Dia=27 mm; Body_Top_Dia_2=23 mm  [stored 0.0754593 ft]; Body_With_Dia=91 mm; Body_With_Dia_1=183 mm; Body_With_Dia_2=183 mm; Bolt_support=562 mm; Bolt_support_2=281 mm; Bolt_support_Dia=20 mm  [stored 0.0656168 ft]; Bolt_support_lenght=145 mm; Bolt_support_lenght_2=155 mm; Bottom_profile=63 mm; D1=160 mm; D3=203 mm; DN=251 mm; Fillet_Length=10 mm  [stored 0.0328084 ft]; Fillet_Length_Ref=30 mm  [stored 0.0984252 ft]; Flange_thickness=22 mm  [stored 0.0721785 ft]; H=854 mm; H3_Ref=844 mm; ID=125 mm; L=730 mm; L_Ref=343 mm; NV_Dia=170 mm; PG_Dia=84 mm; PG_Ref=122 mm; PG_depth=14 mm  [stored 0.0459318 ft]; PG_height=496 mm; PG_height_1=454 mm; PG_ref=135 mm; PR_1=67 mm; P_lenght=103 mm; Pilot_Dia_1=47 mm; Pilot_Dia_2=94 mm; Pilot_Dia_3=31 mm  [stored 0.101706 ft]; Pilot_Dia_4=16 mm  [stored 0.0524934 ft]; Pilot_Dia_5=10 mm  [stored 0.0328084 ft]; Pilot_top_1=506 mm; Pilot_top_ref=126 mm; Profile1_Height=315 mm; Profile1_Length=55 mm; Profile1_Length_2=36 mm; Profile_Dia=10 mm  [stored 0.0328084 ft]; Profile_Dia_2=10 mm  [stored 0.0328084 ft]; Profile_Dia_3=20 mm  [stored 0.0656168 ft]; Profile_Dia_Ref=5 mm  [stored 0.0164042 ft]; Profile_Dia_Ref_2=20 mm  [stored 0.0656168 ft]; Profile_height ref=30 mm  [stored 0.0984252 ft]; T_Height=297 mm; T_Height_2=254 mm; T_Height_Ref_1=42 mm; T_Height_Ref_2=49 mm; T_ref=479 mm; Top_Profile=337 mm; Top_Profile_Ref=342 mm; W=775 mm; W_Ref=761 mm
- 879-0250-10-14400329999_DN250_PN16: Body_Collar_Dia=66 mm; Body_Collar_Dia_2=46 mm; Body_Flange_Dia=209 mm; Body_Flange_Dia_2=228 mm; Body_Height_1=183 mm; Body_Height_2=91 mm; Body_Height_3=81 mm; Body_Height_4=106 mm; Body_Top_Dia=27 mm; Body_Top_Dia_2=23 mm  [stored 0.0754593 ft]; Body_With_Dia=91 mm; Body_With_Dia_1=183 mm; Body_With_Dia_2=183 mm; Bolt_support=562 mm; Bolt_support_2=281 mm; Bolt_support_Dia=20 mm  [stored 0.0656168 ft]; Bolt_support_lenght=145 mm; Bolt_support_lenght_2=155 mm; Bottom_profile=63 mm; D1=160 mm; D3=203 mm; DN=251 mm; Fillet_Length=10 mm  [stored 0.0328084 ft]; Fillet_Length_Ref=30 mm  [stored 0.0984252 ft]; Flange_thickness=22 mm  [stored 0.0721785 ft]; H=850 mm; H3_Ref=840 mm; ID=125 mm; L=730 mm; L_Ref=343 mm; NV_Dia=170 mm; PG_Dia=84 mm; PG_Ref=122 mm; PG_depth=14 mm  [stored 0.0459318 ft]; PG_height=477 mm; PG_height_1=435 mm; PG_ref=135 mm; PR_1=71 mm; P_lenght=101 mm; Pilot_Dia_1=46 mm; Pilot_Dia_2=92 mm; Pilot_Dia_3=31 mm  [stored 0.101706 ft]; Pilot_Dia_4=15 mm  [stored 0.0492126 ft]; Pilot_Dia_5=10 mm  [stored 0.0328084 ft]; Pilot_top_1=504 mm; Pilot_top_ref=124 mm; Profile1_Height=292 mm; Profile1_Length=55 mm; Profile1_Length_2=36 mm; Profile_Dia=10 mm  [stored 0.0328084 ft]; Profile_Dia_2=10 mm  [stored 0.0328084 ft]; Profile_Dia_3=20 mm  [stored 0.0656168 ft]; Profile_Dia_Ref=5 mm  [stored 0.0164042 ft]; Profile_Dia_Ref_2=20 mm  [stored 0.0656168 ft]; Profile_height ref=30 mm  [stored 0.0984252 ft]; T_Height=316 mm; T_Height_2=270 mm; T_Height_Ref_1=45 mm  [stored 0.147638 ft]; T_Height_Ref_2=53 mm; T_ref=465 mm; Top_Profile=337 mm; Top_Profile_Ref=342 mm; W=775 mm; W_Ref=761 mm
- 879-0250-10-14400339999_DN250_PN16: Body_Collar_Dia=66 mm; Body_Collar_Dia_2=46 mm; Body_Flange_Dia=209 mm; Body_Flange_Dia_2=228 mm; Body_Height_1=183 mm; Body_Height_2=91 mm; Body_Height_3=105 mm; Body_Height_4=106 mm; Body_Top_Dia=27 mm; Body_Top_Dia_2=23 mm  [stored 0.0754593 ft]; Body_With_Dia=91 mm; Body_With_Dia_1=183 mm; Body_With_Dia_2=183 mm; Bolt_support=562 mm; Bolt_support_2=281 mm; Bolt_support_Dia=20 mm  [stored 0.0656168 ft]; Bolt_support_lenght=145 mm; Bolt_support_lenght_2=155 mm; Bottom_profile=63 mm; D1=160 mm; D3=203 mm; DN=251 mm; Fillet_Length=10 mm  [stored 0.0328084 ft]; Fillet_Length_Ref=30 mm  [stored 0.0984252 ft]; Flange_thickness=22 mm  [stored 0.0721785 ft]; H=850 mm; H3_Ref=840 mm; ID=125 mm; L=730 mm; L_Ref=343 mm; NV_Dia=170 mm; PG_Dia=84 mm; PG_Ref=122 mm; PG_depth=14 mm  [stored 0.0459318 ft]; PG_height=479 mm; PG_height_1=438 mm; PG_ref=135 mm; PR_1=71 mm; P_lenght=101 mm; Pilot_Dia_1=46 mm; Pilot_Dia_2=92 mm; Pilot_Dia_3=31 mm  [stored 0.101706 ft]; Pilot_Dia_4=15 mm  [stored 0.0492126 ft]; Pilot_Dia_5=10 mm  [stored 0.0328084 ft]; Pilot_top_1=515 mm; Pilot_top_ref=112 mm; Profile1_Height=295 mm; Profile1_Length=55 mm; Profile1_Length_2=36 mm; Profile_Dia=10 mm  [stored 0.0328084 ft]; Profile_Dia_2=10 mm  [stored 0.0328084 ft]; Profile_Dia_3=20 mm  [stored 0.0656168 ft]; Profile_Dia_Ref=5 mm  [stored 0.0164042 ft]; Profile_Dia_Ref_2=20 mm  [stored 0.0656168 ft]; Profile_height ref=30 mm  [stored 0.0984252 ft]; T_Height=313 mm; T_Height_2=268 mm; T_Height_Ref_1=45 mm  [stored 0.147638 ft]; T_Height_Ref_2=52 mm; T_ref=466 mm; Top_Profile=337 mm; Top_Profile_Ref=342 mm; W=775 mm; W_Ref=761 mm

note: [stored X ft] marks values corroborated as IEEE doubles in the binary element streams (Revit-internal decimal feet)

## geometry (parser evidence)
native form markers: Sweep x4
no freeform markers — native parametric forms only
